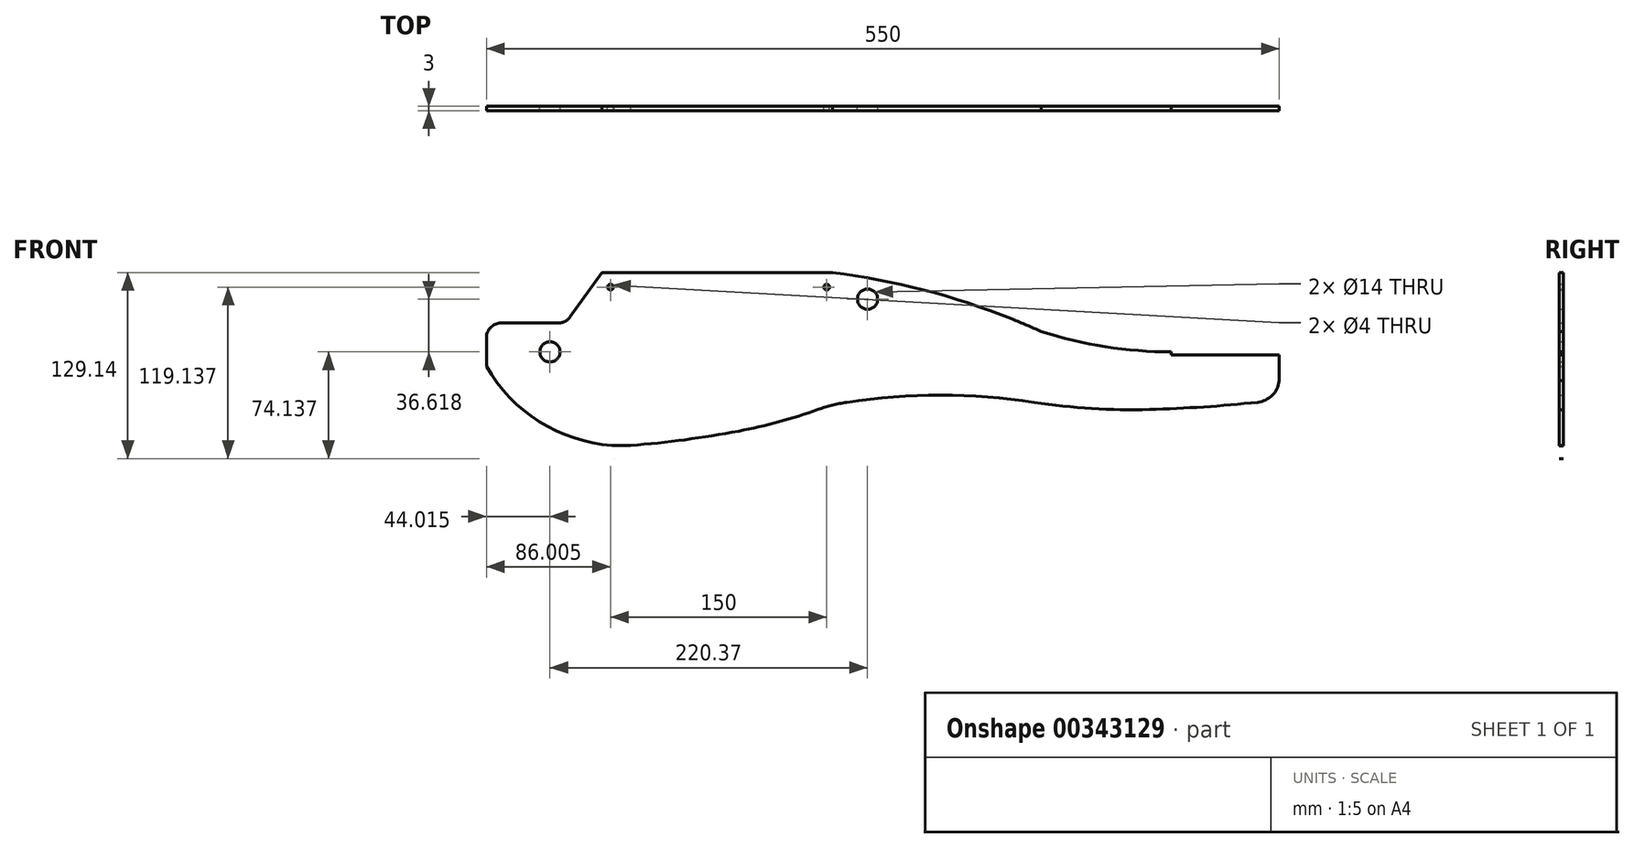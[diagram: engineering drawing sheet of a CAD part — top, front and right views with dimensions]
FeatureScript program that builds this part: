
annotation { "Feature Type Name" : "Feature", "Feature Type Description" : "" }
export const myFeature = defineFeature(function(context is Context, id is Id, definition is map)
    precondition{}
    {
        {
            var Q0;
            Q0=qCreatedBy(makeId("Front.planeOp"),FACE);
            var sketch = newSketch(context, id + "F0", { "sketchPlane" : qUnion([Q0])});
            skLineSegment(sketch, "E0", {"start": v(-85.37, -143.5) * mm, "end": v(-85.3, -135.5) * mm});
            skLineSegment(sketch, "E1", {"start": v(-60.46, -133.63) * mm, "end": v(-59.56, -141.58) * mm});
            skLineSegment(sketch, "E2", {"start": v(-107.58, -141) * mm, "end": v(-106.37, -133.08) * mm});
            skLineSegment(sketch, "E3", {"start": v(-111.58, -131.08) * mm, "end": v(-111.58, -155.3) * mm});
            skLineSegment(sketch, "E4", {"start": v(-19.81, -207.75) * mm, "end": v(-19.81, -42.75) * mm});
            skArc(sketch, "E5", {"start": v(2.74, -207.75) * mm, "mid": v(4.99, -150.27) * mm, "end": v(5.74, -92.75) * mm});
            skLineSegment(sketch, "E6", {"start": v(-164.34, -136.55) * mm, "end": v(-164.34, -172.55) * mm});
            skLineSegment(sketch, "E7", {"start": v(-144.97, -132.55) * mm, "end": v(-144.97, -180.55) * mm});
            skArc(sketch, "E8", {"start": v(-153.84, -148.05) * mm, "mid": v(-164.34, -137.55) * mm, "end": v(-174.84, -148.05) * mm});
            skLineSegment(sketch, "E9", {"start": v(-422.26, -217.75) * mm, "end": v(-422.26, 217.75) * mm});
            skLineSegment(sketch, "E10", {"start": v(242.74, -162.97) * mm, "end": v(242.74, -102.75) * mm});
            skLineSegment(sketch, "E11", {"start": v(254.74, -42.75) * mm, "end": v(254.74, -182.75) * mm});
            skLineSegment(sketch, "E12", {"start": v(-34.1, -204.75) * mm, "end": v(-34.1, -45.75) * mm});
            skLineSegment(sketch, "E13", {"start": v(-408.76, -42.75) * mm, "end": v(-408.76, -207.75) * mm});
            skLineSegment(sketch, "E14", {"start": v(-405.76, -42.75) * mm, "end": v(-405.76, -207.75) * mm});
            skLineSegment(sketch, "E15", {"start": v(-5.76, -42.75) * mm, "end": v(-5.76, -207.75) * mm});
            skLineSegment(sketch, "E16", {"start": v(-8.76, -42.75) * mm, "end": v(-8.76, -207.75) * mm});
            skLineSegment(sketch, "E17", {"start": v(-207.26, -215.75) * mm, "end": v(-207.26, -34.75) * mm});
            skCircle(sketch, "E18", {"center": v(78.1, -143) * mm, "radius": 7 * mm});
            skLineSegment(sketch, "E19", {"start": v(-195.26, -207.75) * mm, "end": v(-195.26, -42.75) * mm});
            skLineSegment(sketch, "E20", {"start": v(-192.26, -42.75) * mm, "end": v(-192.26, -207.75) * mm});
            skLineSegment(sketch, "E21", {"start": v(-219.26, -207.75) * mm, "end": v(-219.26, -42.75) * mm});
            skLineSegment(sketch, "E22", {"start": v(-222.26, -42.75) * mm, "end": v(-222.26, -207.75) * mm});
            skLineSegment(sketch, "E23", {"start": v(-7.26, -42.75) * mm, "end": v(-7.26, -207.75) * mm});
            skLineSegment(sketch, "E24", {"start": v(-407.26, -207.75) * mm, "end": v(-407.26, -42.75) * mm});
            skLineSegment(sketch, "E25", {"start": v(-234, -147.12) * mm, "end": v(-234, -139.24) * mm});
            skLineSegment(sketch, "E26", {"start": v(-394, -147.12) * mm, "end": v(-394, -139.24) * mm});
            skLineSegment(sketch, "E27", {"start": v(2.74, -42.75) * mm, "end": v(2.74, -207.75) * mm});
            skLineSegment(sketch, "E28", {"start": v(407.74, 217.75) * mm, "end": v(407.74, -217.75) * mm});
            skLineSegment(sketch, "E29", {"start": v(-92.77, -153.3) * mm, "end": v(-115.58, -153.3) * mm});
            skLineSegment(sketch, "E30", {"start": v(-407.26, -204.75) * mm, "end": v(-7.26, -204.75) * mm});
            skLineSegment(sketch, "E31", {"start": v(-407.26, -207.75) * mm, "end": v(-7.26, -207.75) * mm});
            skLineSegment(sketch, "E32", {"start": v(-422.26, -217.75) * mm, "end": v(407.74, -217.75) * mm});
            skCircle(sketch, "E33", {"center": v(-271.57, -159.18) * mm, "radius": 7 * mm});
            skLineSegment(sketch, "E34", {"start": v(-394, -148) * mm, "end": v(-234, -148) * mm});
            skLineSegment(sketch, "E35", {"start": v(-234, -172) * mm, "end": v(-394, -172) * mm});
            skLineSegment(sketch, "E36", {"start": v(-386.92, -141) * mm, "end": v(-234, -141) * mm});
            skLineSegment(sketch, "E37", {"start": v(-408.76, -207.75) * mm, "end": v(-407.26, -207.75) * mm});
            skLineSegment(sketch, "E38", {"start": v(-394, -172) * mm, "end": v(-394, -148) * mm});
            skLineSegment(sketch, "E39", {"start": v(-378.87, -172) * mm, "end": v(-384.76, -172) * mm});
            skLineSegment(sketch, "E40", {"start": v(-383, -164.94) * mm, "end": v(-383, -155.08) * mm});
            skLineSegment(sketch, "E41", {"start": v(-378.87, -148) * mm, "end": v(-384.76, -148) * mm});
            skLineSegment(sketch, "E42", {"start": v(-237.26, -202.75) * mm, "end": v(-177.26, -202.75) * mm});
            skLineSegment(sketch, "E43", {"start": v(-237.26, -207.75) * mm, "end": v(-237.26, -202.75) * mm});
            skLineSegment(sketch, "E44", {"start": v(-217.26, -217.75) * mm, "end": v(-217.26, -222.75) * mm});
            skLineSegment(sketch, "E45", {"start": v(-234, -172) * mm, "end": v(-234, -148) * mm});
            skLineSegment(sketch, "E46", {"start": v(-245.64, -157.09) * mm, "end": v(-257.64, -157.09) * mm});
            skLineSegment(sketch, "E47", {"start": v(-257.64, -157.09) * mm, "end": v(-254.38, -155.57) * mm});
            skLineSegment(sketch, "E48", {"start": v(-245.64, -157.09) * mm, "end": v(-248.9, -158.61) * mm});
            skLineSegment(sketch, "E49", {"start": v(-177.26, -202.75) * mm, "end": v(-177.26, -207.75) * mm});
            skLineSegment(sketch, "E50", {"start": v(-139.97, -157.55) * mm, "end": v(-149.97, -157.55) * mm});
            skLineSegment(sketch, "E51", {"start": v(-139.97, -172.55) * mm, "end": v(-149.97, -172.55) * mm});
            skArc(sketch, "E52", {"start": v(-158.84, -172.55) * mm, "mid": v(-155.1, -160.55) * mm, "end": v(-153.84, -148.05) * mm});
            skArc(sketch, "E53", {"start": v(-174.84, -148.05) * mm, "mid": v(-173.57, -160.55) * mm, "end": v(-169.84, -172.55) * mm});
            skLineSegment(sketch, "E54", {"start": v(-168.84, -157.55) * mm, "end": v(-168.84, -172.55) * mm});
            skLineSegment(sketch, "E55", {"start": v(-159.84, -157.55) * mm, "end": v(-159.84, -172.55) * mm});
            skLineSegment(sketch, "E56", {"start": v(-168.84, -172.55) * mm, "end": v(-169.84, -172.55) * mm});
            skLineSegment(sketch, "E57", {"start": v(-151.84, -180.55) * mm, "end": v(-176.84, -180.55) * mm});
            skLineSegment(sketch, "E58", {"start": v(-159.84, -172.55) * mm, "end": v(-158.84, -172.55) * mm});
            skLineSegment(sketch, "E59", {"start": v(-168.84, -175.55) * mm, "end": v(-168.84, -185.55) * mm});
            skLineSegment(sketch, "E60", {"start": v(-159.84, -175.55) * mm, "end": v(-159.84, -185.55) * mm});
            skLineSegment(sketch, "E61", {"start": v(-170.8, -143.7) * mm, "end": v(-168.69, -141.58) * mm});
            skCircle(sketch, "E62", {"center": v(-169.75, -142.65) * mm, "radius": 1 * mm});
            skLineSegment(sketch, "E63", {"start": v(-170.8, -141.58) * mm, "end": v(-168.69, -143.7) * mm});
            skLineSegment(sketch, "E64", {"start": v(-170.8, -152.4) * mm, "end": v(-168.69, -154.52) * mm});
            skCircle(sketch, "E65", {"center": v(-169.75, -153.46) * mm, "radius": 1 * mm});
            skLineSegment(sketch, "E66", {"start": v(-170.8, -154.52) * mm, "end": v(-168.69, -152.4) * mm});
            skLineSegment(sketch, "E67", {"start": v(-175.84, -148.05) * mm, "end": v(-152.84, -148.05) * mm});
            skLineSegment(sketch, "E68", {"start": v(-159.99, -141.58) * mm, "end": v(-157.87, -143.7) * mm});
            skCircle(sketch, "E69", {"center": v(-158.93, -142.65) * mm, "radius": 1 * mm});
            skLineSegment(sketch, "E70", {"start": v(-159.99, -143.7) * mm, "end": v(-157.87, -141.58) * mm});
            skLineSegment(sketch, "E71", {"start": v(-159.84, -157.55) * mm, "end": v(-168.84, -157.55) * mm});
            skCircle(sketch, "E72", {"center": v(-158.93, -153.46) * mm, "radius": 1 * mm});
            skLineSegment(sketch, "E73", {"start": v(-159.99, -154.52) * mm, "end": v(-157.87, -152.4) * mm});
            skLineSegment(sketch, "E74", {"start": v(-159.99, -152.4) * mm, "end": v(-157.87, -154.52) * mm});
            skCircle(sketch, "E75", {"center": v(-164.34, -148.05) * mm, "radius": 3 * mm});
            skCircle(sketch, "E76", {"center": v(-131.73, -173.26) * mm, "radius": 7 * mm});
            skLineSegment(sketch, "E77", {"start": v(2.74, -207.75) * mm, "end": v(225.72, -182.75) * mm});
            skArc(sketch, "E78", {"start": v(-107.58, -141) * mm, "mid": v(-83.7, -153.3) * mm, "end": v(-59.56, -141.58) * mm});
            skArc(sketch, "E79", {"start": v(-91.87, -143.25) * mm, "mid": v(-88.62, -143.43) * mm, "end": v(-85.37, -143.5) * mm});
            skArc(sketch, "E80", {"start": v(-90.32, -152.49) * mm, "mid": v(-87.93, -151.15) * mm, "end": v(-89.13, -148.68) * mm});
            skArc(sketch, "E81", {"start": v(-91.84, -143.25) * mm, "mid": v(-93.94, -144.78) * mm, "end": v(-92.77, -147.1) * mm});
            skLineSegment(sketch, "E82", {"start": v(-92.77, -147.1) * mm, "end": v(-89.07, -148.7) * mm});
            skLineSegment(sketch, "E83", {"start": v(-7.26, -217.75) * mm, "end": v(-7.26, -222.75) * mm});
            skLineSegment(sketch, "E84", {"start": v(-5.76, -207.75) * mm, "end": v(-7.26, -207.75) * mm});
            skLineSegment(sketch, "E85", {"start": v(89.26, -209.17) * mm, "end": v(189.26, -209.17) * mm});
            skLineSegment(sketch, "E86", {"start": v(89.26, -211.17) * mm, "end": v(189.26, -211.17) * mm});
            skLineSegment(sketch, "E87", {"start": v(89.26, -210.17) * mm, "end": v(189.26, -210.17) * mm});
            skLineSegment(sketch, "E88", {"start": v(89.26, -209.17) * mm, "end": v(89.26, -206.67) * mm});
            skLineSegment(sketch, "E89", {"start": v(89.26, -211.17) * mm, "end": v(89.26, -209.17) * mm});
            skLineSegment(sketch, "E90", {"start": v(94.26, -211.17) * mm, "end": v(94.26, -209.17) * mm});
            skLineSegment(sketch, "E91", {"start": v(93.26, -211.17) * mm, "end": v(93.26, -209.17) * mm});
            skLineSegment(sketch, "E92", {"start": v(92.26, -211.17) * mm, "end": v(92.26, -209.17) * mm});
            skLineSegment(sketch, "E93", {"start": v(91.26, -211.17) * mm, "end": v(91.26, -209.17) * mm});
            skLineSegment(sketch, "E94", {"start": v(90.26, -211.17) * mm, "end": v(90.26, -209.17) * mm});
            skLineSegment(sketch, "E95", {"start": v(99.26, -211.17) * mm, "end": v(99.26, -206.67) * mm});
            skLineSegment(sketch, "E96", {"start": v(98.26, -211.17) * mm, "end": v(98.26, -209.17) * mm});
            skLineSegment(sketch, "E97", {"start": v(109.26, -211.17) * mm, "end": v(109.26, -206.67) * mm});
            skLineSegment(sketch, "E98", {"start": v(97.26, -211.17) * mm, "end": v(97.26, -209.17) * mm});
            skLineSegment(sketch, "E99", {"start": v(96.26, -211.17) * mm, "end": v(96.26, -209.17) * mm});
            skLineSegment(sketch, "E100", {"start": v(95.26, -211.17) * mm, "end": v(95.26, -209.17) * mm});
            skLineSegment(sketch, "E101", {"start": v(129.26, -211.17) * mm, "end": v(129.26, -206.67) * mm});
            skLineSegment(sketch, "E102", {"start": v(119.26, -211.17) * mm, "end": v(119.26, -206.67) * mm});
            skLineSegment(sketch, "E103", {"start": v(72.73, -162.02) * mm, "end": v(76, -160.5) * mm});
            skLineSegment(sketch, "E104", {"start": v(84.73, -162.02) * mm, "end": v(72.73, -162.02) * mm});
            skLineSegment(sketch, "E105", {"start": v(84.73, -162.02) * mm, "end": v(81.47, -163.54) * mm});
            skLineSegment(sketch, "E106", {"start": v(149.26, -211.17) * mm, "end": v(149.26, -206.67) * mm});
            skLineSegment(sketch, "E107", {"start": v(139.26, -211.17) * mm, "end": v(139.26, -206.67) * mm});
            skLineSegment(sketch, "E108", {"start": v(159.26, -211.17) * mm, "end": v(159.26, -206.67) * mm});
            skLineSegment(sketch, "E109", {"start": v(169.26, -211.17) * mm, "end": v(169.26, -206.67) * mm});
            skLineSegment(sketch, "E110", {"start": v(202.74, -217.75) * mm, "end": v(202.74, -222.75) * mm});
            skLineSegment(sketch, "E111", {"start": v(189.26, -211.17) * mm, "end": v(189.26, -206.67) * mm});
            skLineSegment(sketch, "E112", {"start": v(179.26, -211.17) * mm, "end": v(179.26, -206.67) * mm});
            skLineSegment(sketch, "E113", {"start": v(222.74, -162.97) * mm, "end": v(236.88, -177.12) * mm});
            skArc(sketch, "E114", {"start": v(225.72, -182.75) * mm, "mid": v(237.9, -176.02) * mm, "end": v(242.74, -162.97) * mm});
            skLineSegment(sketch, "E115", {"start": v(244.74, -182.75) * mm, "end": v(254.74, -182.75) * mm});
            skLineSegment(sketch, "E116", {"start": v(222.74, -160.47) * mm, "end": v(222.74, -165.47) * mm});
            skLineSegment(sketch, "E117", {"start": v(225.24, -162.97) * mm, "end": v(220.24, -162.97) * mm});
            skLineSegment(sketch, "E118", {"start": v(-57.56, -128.27) * mm, "end": v(-109.58, -128.27) * mm});
            skLineSegment(sketch, "E119", {"start": v(-107.58, -133.08) * mm, "end": v(-115.58, -133.08) * mm});
            skLineSegment(sketch, "E120", {"start": v(168.53, 19.16) * mm, "end": v(-411.1, 19.16) * mm});
            skLineSegment(sketch, "E121", {"start": v(-103.29, 50.21) * mm, "end": v(-113.06, 50.21) * mm});
            skLineSegment(sketch, "E122", {"start": v(-103.29, 65.21) * mm, "end": v(-113.06, 65.21) * mm});
            skLineSegment(sketch, "E123", {"start": v(85.41, 128) * mm, "end": v(-332.58, 128) * mm});
            skLineSegment(sketch, "E124", {"start": v(-384.59, 86.54) * mm, "end": v(-80.66, 86.54) * mm});
            skLineSegment(sketch, "E125", {"start": v(-407.26, -17.75) * mm, "end": v(-7.26, -17.75) * mm});
            skLineSegment(sketch, "E126", {"start": v(-407.26, -45.75) * mm, "end": v(-7.26, -45.75) * mm});
            skLineSegment(sketch, "E127", {"start": v(-407.26, -42.75) * mm, "end": v(-7.26, -42.75) * mm});
            skArc(sketch, "E128", {"start": v(-20.12, 150.85) * mm, "mid": v(-81.3, 171) * mm, "end": v(-144.59, 183) * mm});
            skLineSegment(sketch, "E129", {"start": v(-144.59, 23.66) * mm, "end": v(165.41, 23.66) * mm});
            skLineSegment(sketch, "E130", {"start": v(-144.59, 17.66) * mm, "end": v(165.41, 17.66) * mm});
            skLineSegment(sketch, "E131", {"start": v(-144.59, 14.66) * mm, "end": v(165.41, 14.66) * mm});
            skLineSegment(sketch, "E132", {"start": v(-384.59, 203) * mm, "end": v(165.41, 203) * mm});
            skLineSegment(sketch, "E133", {"start": v(-122.26, 183) * mm, "end": v(150.8, 183) * mm});
            skLineSegment(sketch, "E134", {"start": v(165.41, 20.66) * mm, "end": v(-144.59, 20.66) * mm});
            skArc(sketch, "E135", {"start": v(-4.59, 93) * mm, "mid": v(-69.59, 98) * mm, "end": v(-134.59, 93) * mm});
            skLineSegment(sketch, "E136", {"start": v(-422.26, 217.75) * mm, "end": v(407.74, 217.75) * mm});
            skArc(sketch, "E137", {"start": v(-291.3, 70.87) * mm, "mid": v(-291.16, 70.87) * mm, "end": v(-291.02, 70.87) * mm});
            skArc(sketch, "E138", {"start": v(-280.24, 144.1) * mm, "mid": v(-309.44, 100) * mm, "end": v(-270.46, 64.26) * mm});
            skArc(sketch, "E139", {"start": v(-384.59, 118) * mm, "mid": v(-358.64, 87.23) * mm, "end": v(-323.25, 68.04) * mm});
            skLineSegment(sketch, "E140", {"start": v(-384.59, 115) * mm, "end": v(-384.59, 47.16) * mm});
            skArc(sketch, "E141", {"start": v(-284.59, 63) * mm, "mid": v(-246.95, 66.98) * mm, "end": v(-209.59, 73) * mm});
            skArc(sketch, "E142", {"start": v(-313.3, 65.36) * mm, "mid": v(-289.43, 53.06) * mm, "end": v(-265.28, 64.79) * mm});
            skLineSegment(sketch, "E143", {"start": v(-286.92, -7.87) * mm, "end": v(-258.15, -7.87) * mm});
            skLineSegment(sketch, "E144", {"start": v(-264.24, 46.33) * mm, "end": v(-274.59, 33.66) * mm});
            skLineSegment(sketch, "E145", {"start": v(-284.59, 13.66) * mm, "end": v(-264.59, 13.66) * mm});
            skLineSegment(sketch, "E146", {"start": v(-284.59, 33.66) * mm, "end": v(-264.59, 33.66) * mm});
            skLineSegment(sketch, "E147", {"start": v(-274.59, 9.66) * mm, "end": v(-264.59, 9.66) * mm});
            skLineSegment(sketch, "E148", {"start": v(-272.59, 5.66) * mm, "end": v(-266.59, 5.66) * mm});
            skArc(sketch, "E149", {"start": v(-234, -102.2) * mm, "mid": v(-288.67, -92.34) * mm, "end": v(-344, -87.2) * mm});
            skLineSegment(sketch, "E150", {"start": v(-394, -102.2) * mm, "end": v(-234, -102.2) * mm});
            skArc(sketch, "E151", {"start": v(-233.33, -99.28) * mm, "mid": v(-288.26, -89.37) * mm, "end": v(-343.84, -84.21) * mm});
            skLineSegment(sketch, "E152", {"start": v(-389.62, -99.2) * mm, "end": v(-248.04, -99.2) * mm});
            skLineSegment(sketch, "E153", {"start": v(-284.59, 14.66) * mm, "end": v(-264.59, 14.66) * mm});
            skLineSegment(sketch, "E154", {"start": v(-284.59, 17.66) * mm, "end": v(-264.59, 17.66) * mm});
            skLineSegment(sketch, "E155", {"start": v(-284.59, 23.66) * mm, "end": v(-264.59, 23.66) * mm});
            skLineSegment(sketch, "E156", {"start": v(-264.59, 20.66) * mm, "end": v(-284.59, 20.66) * mm});
            skLineSegment(sketch, "E157", {"start": v(-407.26, -39.75) * mm, "end": v(-407.26, -14.75) * mm});
            skArc(sketch, "E158", {"start": v(-344, -87.2) * mm, "mid": v(-370.3, -90.35) * mm, "end": v(-394, -102.2) * mm});
            skArc(sketch, "E159", {"start": v(-343.84, -84.21) * mm, "mid": v(-370.27, -87.22) * mm, "end": v(-394.26, -98.7) * mm});
            skLineSegment(sketch, "E160", {"start": v(-390.25, -83.08) * mm, "end": v(-394.4, -99.99) * mm});
            skLineSegment(sketch, "E161", {"start": v(-393.47, -98.16) * mm, "end": v(-391.72, -100.59) * mm});
            skArc(sketch, "E162", {"start": v(-394.26, -98.7) * mm, "mid": v(-395.13, -100.54) * mm, "end": v(-394, -102.2) * mm});
            skLineSegment(sketch, "E163", {"start": v(-407.26, -42.75) * mm, "end": v(-408.76, -42.75) * mm});
            skLineSegment(sketch, "E164", {"start": v(-407.26, -42.75) * mm, "end": v(-405.26, -42.75) * mm});
            skLineSegment(sketch, "E165", {"start": v(-390.25, -83.08) * mm, "end": v(-381.94, -83.08) * mm});
            skLineSegment(sketch, "E166", {"start": v(-303.46, -80.13) * mm, "end": v(-305.53, -88.59) * mm});
            skLineSegment(sketch, "E167", {"start": v(-320.4, -100.94) * mm, "end": v(-303.46, -80.13) * mm});
            skLineSegment(sketch, "E168", {"start": v(-303.46, -80.13) * mm, "end": v(-278.38, -80.13) * mm});
            skLineSegment(sketch, "E169", {"start": v(-385.2, 31) * mm, "end": v(-314.86, 31) * mm});
            skLineSegment(sketch, "E170", {"start": v(-373.46, 14.66) * mm, "end": v(-304.59, 14.66) * mm});
            skLineSegment(sketch, "E171", {"start": v(-373.3, 23.66) * mm, "end": v(-304.59, 23.66) * mm});
            skLineSegment(sketch, "E172", {"start": v(-373.4, 17.66) * mm, "end": v(-304.59, 17.66) * mm});
            skLineSegment(sketch, "E173", {"start": v(-304.59, 20.66) * mm, "end": v(-373.36, 20.66) * mm});
            skLineSegment(sketch, "E174", {"start": v(-403.86, 18.63) * mm, "end": v(-403.81, 20.73) * mm});
            skLineSegment(sketch, "E175", {"start": v(-400.92, 18.57) * mm, "end": v(-400.88, 20.67) * mm});
            skLineSegment(sketch, "E176", {"start": v(-411.1, 19.8) * mm, "end": v(-352.96, 18.78) * mm});
            skLineSegment(sketch, "E177", {"start": v(-374.7, 29.16) * mm, "end": v(-375.06, 9.16) * mm});
            skLineSegment(sketch, "E178", {"start": v(-373.2, 29.13) * mm, "end": v(-373.56, 9.14) * mm});
            skLineSegment(sketch, "E179", {"start": v(-374.72, 28.16) * mm, "end": v(-375.04, 10.16) * mm});
            skLineSegment(sketch, "E180", {"start": v(-377.34, 10.2) * mm, "end": v(-377.02, 28.2) * mm});
            skLineSegment(sketch, "E181", {"start": v(-387, 12.22) * mm, "end": v(-386.76, 26.52) * mm});
            skLineSegment(sketch, "E182", {"start": v(-394.4, 12.35) * mm, "end": v(-394.15, 26.65) * mm});
            skLineSegment(sketch, "E183", {"start": v(-400.97, 15.42) * mm, "end": v(-398.47, 15.37) * mm});
            skLineSegment(sketch, "E184", {"start": v(-400.82, 23.82) * mm, "end": v(-398.33, 23.77) * mm});
            skLineSegment(sketch, "E185", {"start": v(-400.97, 15.42) * mm, "end": v(-400.82, 23.82) * mm});
            skLineSegment(sketch, "E186", {"start": v(-403.21, 17.76) * mm, "end": v(-403.14, 21.56) * mm});
            skLineSegment(sketch, "E187", {"start": v(-403.14, 21.56) * mm, "end": v(-400.86, 21.52) * mm});
            skLineSegment(sketch, "E188", {"start": v(-403.21, 17.76) * mm, "end": v(-400.93, 17.72) * mm});
            skLineSegment(sketch, "E189", {"start": v(-382.12, 14.29) * mm, "end": v(-381.94, 24.29) * mm});
            skLineSegment(sketch, "E190", {"start": v(-386.83, 22.37) * mm, "end": v(-381.98, 22.28) * mm});
            skLineSegment(sketch, "E191", {"start": v(-398.47, 15.37) * mm, "end": v(-398.33, 23.77) * mm});
            skLineSegment(sketch, "E192", {"start": v(-381.94, 24.29) * mm, "end": v(-377.1, 24.2) * mm});
            skLineSegment(sketch, "E193", {"start": v(-394.15, 26.65) * mm, "end": v(-386.76, 26.52) * mm});
            skLineSegment(sketch, "E194", {"start": v(-377.02, 28.2) * mm, "end": v(-374.72, 28.16) * mm});
            skLineSegment(sketch, "E195", {"start": v(-382.12, 14.29) * mm, "end": v(-377.27, 14.2) * mm});
            skLineSegment(sketch, "E196", {"start": v(-395.8, 18.03) * mm, "end": v(-395.75, 21.03) * mm});
            skLineSegment(sketch, "E197", {"start": v(-396.8, 18.04) * mm, "end": v(-396.75, 21.04) * mm});
            skLineSegment(sketch, "E198", {"start": v(-395.75, 21.03) * mm, "end": v(-394.25, 21) * mm});
            skLineSegment(sketch, "E199", {"start": v(-398.37, 21.47) * mm, "end": v(-396.75, 21.04) * mm});
            skLineSegment(sketch, "E200", {"start": v(-396.8, 18.8) * mm, "end": v(-395.8, 18.78) * mm});
            skLineSegment(sketch, "E201", {"start": v(-396.77, 20.3) * mm, "end": v(-395.77, 20.28) * mm});
            skLineSegment(sketch, "E202", {"start": v(-386.93, 16.38) * mm, "end": v(-382.08, 16.3) * mm});
            skLineSegment(sketch, "E203", {"start": v(-395.8, 18.03) * mm, "end": v(-394.3, 18) * mm});
            skLineSegment(sketch, "E204", {"start": v(-398.43, 17.67) * mm, "end": v(-396.8, 18.04) * mm});
            skLineSegment(sketch, "E205", {"start": v(-394.4, 12.35) * mm, "end": v(-387, 12.22) * mm});
            skLineSegment(sketch, "E206", {"start": v(-377.34, 10.2) * mm, "end": v(-375.04, 10.16) * mm});
            skLineSegment(sketch, "E207", {"start": v(-384.59, 23.66) * mm, "end": v(-384.59, 14.66) * mm});
            skLineSegment(sketch, "E208", {"start": v(-401.47, -2.69) * mm, "end": v(-400.92, 18.57) * mm});
            skLineSegment(sketch, "E209", {"start": v(-403.86, 18.63) * mm, "end": v(-403.87, -3.74) * mm});
            skLineSegment(sketch, "E210", {"start": v(-375.06, 9.16) * mm, "end": v(-373.56, 9.14) * mm});
            skLineSegment(sketch, "E211", {"start": v(-384.59, 14.66) * mm, "end": v(-374.96, 14.66) * mm});
            skLineSegment(sketch, "E212", {"start": v(-400.63, 49.57) * mm, "end": v(-400.88, 20.68) * mm});
            skLineSegment(sketch, "E213", {"start": v(-403.82, 20.73) * mm, "end": v(-402.8, 50.28) * mm});
            skLineSegment(sketch, "E214", {"start": v(-385.2, 31) * mm, "end": v(-388.81, 26.59) * mm});
            skLineSegment(sketch, "E215", {"start": v(-374.7, 29.16) * mm, "end": v(-373.2, 29.13) * mm});
            skLineSegment(sketch, "E216", {"start": v(-384.59, 23.66) * mm, "end": v(-374.8, 23.66) * mm});
            skLineSegment(sketch, "E217", {"start": v(-292.43, 24.5) * mm, "end": v(-292.43, 12.5) * mm});
            skLineSegment(sketch, "E218", {"start": v(-304.59, 4.16) * mm, "end": v(-304.59, 34.16) * mm});
            skLineSegment(sketch, "E219", {"start": v(-284.59, 34.16) * mm, "end": v(-284.59, 4.16) * mm});
            skLineSegment(sketch, "E220", {"start": v(-300.59, 4.16) * mm, "end": v(-300.59, 34.16) * mm});
            skLineSegment(sketch, "E221", {"start": v(-296.59, 34.16) * mm, "end": v(-296.59, 4.16) * mm});
            skLineSegment(sketch, "E222", {"start": v(-337.09, 20.66) * mm, "end": v(-337.09, 17.66) * mm});
            skLineSegment(sketch, "E223", {"start": v(-342.09, 20.66) * mm, "end": v(-342.09, 17.66) * mm});
            skCircle(sketch, "E224", {"center": v(-313.37, 6.52) * mm, "radius": 7 * mm});
            skLineSegment(sketch, "E225", {"start": v(-286.92, -7.87) * mm, "end": v(-298.59, 1.66) * mm});
            skLineSegment(sketch, "E226", {"start": v(-284.59, 4.16) * mm, "end": v(-304.59, 4.16) * mm});
            skLineSegment(sketch, "E227", {"start": v(-296.59, 4.16) * mm, "end": v(-296.59, 1.66) * mm});
            skLineSegment(sketch, "E228", {"start": v(-300.59, 4.16) * mm, "end": v(-300.59, 1.66) * mm});
            skLineSegment(sketch, "E229", {"start": v(-296.59, 1.66) * mm, "end": v(-300.59, 1.66) * mm});
            skLineSegment(sketch, "E230", {"start": v(-292.43, 12.5) * mm, "end": v(-293.95, 15.76) * mm});
            skLineSegment(sketch, "E231", {"start": v(-274.59, 9.66) * mm, "end": v(-274.59, 13.66) * mm});
            skLineSegment(sketch, "E232", {"start": v(-274.59, 11.66) * mm, "end": v(-277.59, 11.66) * mm});
            skLineSegment(sketch, "E233", {"start": v(-277.59, 11.66) * mm, "end": v(-277.59, 13.66) * mm});
            skLineSegment(sketch, "E234", {"start": v(-272.59, 5.66) * mm, "end": v(-272.59, 9.66) * mm});
            skArc(sketch, "E235", {"start": v(-323.25, 68.04) * mm, "mid": v(-304.15, 63.77) * mm, "end": v(-284.59, 63) * mm});
            skLineSegment(sketch, "E236", {"start": v(-292.43, 24.5) * mm, "end": v(-290.91, 21.23) * mm});
            skLineSegment(sketch, "E237", {"start": v(-304.59, 34.16) * mm, "end": v(-284.59, 34.16) * mm});
            skLineSegment(sketch, "E238", {"start": v(-296.59, 36.66) * mm, "end": v(-296.59, 34.16) * mm});
            skLineSegment(sketch, "E239", {"start": v(-300.59, 36.66) * mm, "end": v(-300.59, 34.16) * mm});
            skLineSegment(sketch, "E240", {"start": v(-300.59, 36.66) * mm, "end": v(-296.59, 36.66) * mm});
            skArc(sketch, "E241", {"start": v(-296.04, 53.88) * mm, "mid": v(-296.02, 53.88) * mm, "end": v(-296, 53.87) * mm});
            skLineSegment(sketch, "E242", {"start": v(-294.84, 57.69) * mm, "end": v(-294.78, 57.66) * mm});
            skArc(sketch, "E243", {"start": v(-297.56, 63.12) * mm, "mid": v(-297.57, 63.12) * mm, "end": v(-297.59, 63.12) * mm});
            skLineSegment(sketch, "E244", {"start": v(-291.02, 70.69) * mm, "end": v(-291.02, 70.87) * mm});
            skCircle(sketch, "E245", {"center": v(-178.82, -29.52) * mm, "radius": 7 * mm});
            skLineSegment(sketch, "E246", {"start": v(-167.26, -35.68) * mm, "end": v(-167.26, -28.6) * mm});
            skLineSegment(sketch, "E247", {"start": v(-222.26, -40.75) * mm, "end": v(-222.26, -29.75) * mm});
            skLineSegment(sketch, "E248", {"start": v(-192.26, -40.75) * mm, "end": v(-192.26, -29.75) * mm});
            skLineSegment(sketch, "E249", {"start": v(-230.2, -56.53) * mm, "end": v(-184.33, -56.53) * mm});
            skLineSegment(sketch, "E250", {"start": v(-237.26, -47.75) * mm, "end": v(-177.26, -47.75) * mm});
            skCircle(sketch, "E251", {"center": v(-258, -112.32) * mm, "radius": 7 * mm});
            skLineSegment(sketch, "E252", {"start": v(-262.84, -107.28) * mm, "end": v(-269.08, -100.79) * mm});
            skLineSegment(sketch, "E253", {"start": v(-233.33, -99.28) * mm, "end": v(-234, -102.2) * mm});
            skLineSegment(sketch, "E254", {"start": v(-236.26, -98.63) * mm, "end": v(-236.92, -101.55) * mm});
            skLineSegment(sketch, "E255", {"start": v(-237.32, -90.65) * mm, "end": v(-234.94, -100.3) * mm});
            skLineSegment(sketch, "E256", {"start": v(-245.93, -90.65) * mm, "end": v(-237.32, -90.65) * mm});
            skLineSegment(sketch, "E257", {"start": v(-237.26, -49.75) * mm, "end": v(-237.26, -59.53) * mm});
            skLineSegment(sketch, "E258", {"start": v(-237.26, -42.75) * mm, "end": v(-237.26, -47.75) * mm});
            skLineSegment(sketch, "E259", {"start": v(-139.97, -137.55) * mm, "end": v(-149.97, -137.55) * mm});
            skLineSegment(sketch, "E260", {"start": v(-149.34, -132.9) * mm, "end": v(-179.34, -132.9) * mm});
            skLineSegment(sketch, "E261", {"start": v(-174.34, -127.9) * mm, "end": v(-174.34, -137.9) * mm});
            skLineSegment(sketch, "E262", {"start": v(-154.34, -127.88) * mm, "end": v(-154.34, -137.88) * mm});
            skCircle(sketch, "E263", {"center": v(-180.24, -96.46) * mm, "radius": 7 * mm});
            skLineSegment(sketch, "E264", {"start": v(-110.07, -90.7) * mm, "end": v(-113.33, -92.22) * mm});
            skLineSegment(sketch, "E265", {"start": v(-122.07, -90.7) * mm, "end": v(-118.8, -89.18) * mm});
            skLineSegment(sketch, "E266", {"start": v(-110.07, -90.7) * mm, "end": v(-122.07, -90.7) * mm});
            skLineSegment(sketch, "E267", {"start": v(-167.26, -54.82) * mm, "end": v(-167.26, -61.9) * mm});
            skLineSegment(sketch, "E268", {"start": v(-175.26, -47.75) * mm, "end": v(-165.5, -47.75) * mm});
            skLineSegment(sketch, "E269", {"start": v(-177.26, -49.75) * mm, "end": v(-177.26, -59.53) * mm});
            skLineSegment(sketch, "E270", {"start": v(-177.26, -47.75) * mm, "end": v(-177.26, -42.75) * mm});
            skLineSegment(sketch, "E271", {"start": v(-167.26, -47.75) * mm, "end": v(-167.26, -42.75) * mm});
            skCircle(sketch, "E272", {"center": v(-116.7, -71.68) * mm, "radius": 7 * mm});
            skLineSegment(sketch, "E273", {"start": v(-244.59, 23.66) * mm, "end": v(-164.59, 23.66) * mm});
            skLineSegment(sketch, "E274", {"start": v(-244.59, 17.66) * mm, "end": v(-164.59, 17.66) * mm});
            skLineSegment(sketch, "E275", {"start": v(-244.59, 14.66) * mm, "end": v(-164.59, 14.66) * mm});
            skLineSegment(sketch, "E276", {"start": v(-164.59, 20.66) * mm, "end": v(-244.59, 20.66) * mm});
            skLineSegment(sketch, "E277", {"start": v(-234.6, 28.66) * mm, "end": v(-234.6, 4.66) * mm});
            skLineSegment(sketch, "E278", {"start": v(-264.59, 4.16) * mm, "end": v(-264.59, 34.16) * mm});
            skLineSegment(sketch, "E279", {"start": v(-244.59, 34.16) * mm, "end": v(-244.59, 4.16) * mm});
            skLineSegment(sketch, "E280", {"start": v(-244.59, 4.16) * mm, "end": v(-264.59, 4.16) * mm});
            skLineSegment(sketch, "E281", {"start": v(-266.59, 5.66) * mm, "end": v(-266.59, 9.66) * mm});
            skLineSegment(sketch, "E282", {"start": v(-244.59, 4.66) * mm, "end": v(-234.6, 4.66) * mm});
            skLineSegment(sketch, "E283", {"start": v(-199.33, -32.75) * mm, "end": v(-215.2, -32.75) * mm});
            skLineSegment(sketch, "E284", {"start": v(-264.24, 46.33) * mm, "end": v(-208.56, 46.33) * mm});
            skLineSegment(sketch, "E285", {"start": v(-264.24, 46.33) * mm, "end": v(-239.6, 32.66) * mm});
            skLineSegment(sketch, "E286", {"start": v(-264.59, 34.16) * mm, "end": v(-244.59, 34.16) * mm});
            skLineSegment(sketch, "E287", {"start": v(-257.51, 26.66) * mm, "end": v(-251.66, 26.66) * mm});
            skLineSegment(sketch, "E288", {"start": v(-244.6, 24.66) * mm, "end": v(-230.6, 24.66) * mm});
            skLineSegment(sketch, "E289", {"start": v(-230.6, 24.66) * mm, "end": v(-230.6, 23.66) * mm});
            skLineSegment(sketch, "E290", {"start": v(-244.6, 28.66) * mm, "end": v(-234.6, 28.66) * mm});
            skLineSegment(sketch, "E291", {"start": v(-242.6, 32.66) * mm, "end": v(-242.6, 28.66) * mm});
            skLineSegment(sketch, "E292", {"start": v(-242.6, 32.66) * mm, "end": v(-236.6, 32.66) * mm});
            skLineSegment(sketch, "E293", {"start": v(-236.6, 32.66) * mm, "end": v(-236.6, 28.66) * mm});
            skLineSegment(sketch, "E294", {"start": v(-234.6, 23.66) * mm, "end": v(-230.6, 23.66) * mm});
            skLineSegment(sketch, "E295", {"start": v(-133.78, 1.66) * mm, "end": v(-133.78, 36.66) * mm});
            skLineSegment(sketch, "E296", {"start": v(-164.59, 4.16) * mm, "end": v(-164.59, 34.16) * mm});
            skLineSegment(sketch, "E297", {"start": v(-144.59, 34.16) * mm, "end": v(-144.59, 4.16) * mm});
            skLineSegment(sketch, "E298", {"start": v(-150.59, 4.16) * mm, "end": v(-150.59, 34.16) * mm});
            skLineSegment(sketch, "E299", {"start": v(-146.59, 34.16) * mm, "end": v(-146.59, 4.16) * mm});
            skLineSegment(sketch, "E300", {"start": v(-156.63, 4.16) * mm, "end": v(-156.63, 34.16) * mm});
            skLineSegment(sketch, "E301", {"start": v(-146.59, 1.66) * mm, "end": v(-150.59, 1.66) * mm});
            skLineSegment(sketch, "E302", {"start": v(-144.59, 4.16) * mm, "end": v(-164.59, 4.16) * mm});
            skLineSegment(sketch, "E303", {"start": v(-150.59, 4.16) * mm, "end": v(-150.59, 1.66) * mm});
            skLineSegment(sketch, "E304", {"start": v(-143.78, 1.66) * mm, "end": v(-131.78, 1.66) * mm});
            skLineSegment(sketch, "E305", {"start": v(-146.59, 4.16) * mm, "end": v(-146.59, 1.66) * mm});
            skLineSegment(sketch, "E306", {"start": v(-152.42, 41.36) * mm, "end": v(-148.59, 36.66) * mm});
            skLineSegment(sketch, "E307", {"start": v(-150.59, 36.66) * mm, "end": v(-146.59, 36.66) * mm});
            skLineSegment(sketch, "E308", {"start": v(-164.59, 34.16) * mm, "end": v(-144.59, 34.16) * mm});
            skLineSegment(sketch, "E309", {"start": v(-184.37, 41.36) * mm, "end": v(-152.42, 41.36) * mm});
            skLineSegment(sketch, "E310", {"start": v(-150.59, 36.66) * mm, "end": v(-150.59, 34.16) * mm});
            skLineSegment(sketch, "E311", {"start": v(-143.78, 36.66) * mm, "end": v(-131.78, 36.66) * mm});
            skLineSegment(sketch, "E312", {"start": v(-146.59, 36.66) * mm, "end": v(-146.59, 34.16) * mm});
            skLineSegment(sketch, "E313", {"start": v(-111.29, 43.14) * mm, "end": v(-111.29, 36.07) * mm});
            skLineSegment(sketch, "E314", {"start": v(-111.29, 50.21) * mm, "end": v(-111.29, 65.21) * mm});
            skLineSegment(sketch, "E315", {"start": v(-144.59, 183) * mm, "end": v(-280.24, 144.1) * mm});
            skArc(sketch, "E316", {"start": v(-330.16, 149.12) * mm, "mid": v(-295.52, 152.48) * mm, "end": v(-278.81, 183) * mm});
            skLineSegment(sketch, "E317", {"start": v(-304.59, 183) * mm, "end": v(-144.59, 183) * mm});
            skLineSegment(sketch, "E318", {"start": v(-384.59, 193) * mm, "end": v(-144.59, 193) * mm});
            skLineSegment(sketch, "E319", {"start": v(-406.06, 197.82) * mm, "end": v(-401.25, 136.7) * mm});
            skLineSegment(sketch, "E320", {"start": v(-404.18, 136.49) * mm, "end": v(-407.41, 197.34) * mm});
            skFitSpline(sketch, "E321", {"points": [v(-407.41, 197.34) * mm, v(-407.4, 197.57) * mm, v(-407.4, 197.87) * mm, v(-407.38, 198.27) * mm, v(-407.25, 198.59) * mm, v(-406.94, 198.85) * mm, v(-406.57, 198.94) * mm, v(-406.2, 198.82) * mm, v(-406.1, 198.34) * mm, v(-406.07, 198) * mm, v(-406.06, 197.82) * mm]});
            skLineSegment(sketch, "E322", {"start": v(-404.03, 134.4) * mm, "end": v(-398.76, 73.68) * mm});
            skLineSegment(sketch, "E323", {"start": v(-397.36, 73.4) * mm, "end": v(-401.1, 134.59) * mm});
            skFitSpline(sketch, "E324", {"points": [v(-398.76, 73.68) * mm, v(-398.73, 73.45) * mm, v(-398.68, 73.16) * mm, v(-398.6, 72.76) * mm, v(-398.43, 72.47) * mm, v(-398.08, 72.26) * mm, v(-397.71, 72.2) * mm, v(-397.36, 72.39) * mm, v(-397.32, 72.88) * mm, v(-397.35, 73.2) * mm, v(-397.36, 73.4) * mm]});
            skLineSegment(sketch, "E325", {"start": v(-401.25, 136.7) * mm, "end": v(-401.1, 134.6) * mm});
            skLineSegment(sketch, "E326", {"start": v(-404.18, 136.49) * mm, "end": v(-404.03, 134.4) * mm});
            skLineSegment(sketch, "E327", {"start": v(-384.59, 144) * mm, "end": v(-384.59, 194.77) * mm});
            skLineSegment(sketch, "E328", {"start": v(-304.59, 181) * mm, "end": v(-304.59, 156.24) * mm});
            skLineSegment(sketch, "E329", {"start": v(-287.59, 173) * mm, "end": v(-287.59, 183) * mm});
            skLineSegment(sketch, "E330", {"start": v(-304.59, 183) * mm, "end": v(-326.6, 152.2) * mm});
            skLineSegment(sketch, "E331", {"start": v(-298.59, 178) * mm, "end": v(-298.59, 166) * mm});
            skLineSegment(sketch, "E332", {"start": v(-348.58, 128) * mm, "end": v(-412.77, 128) * mm});
            skLineSegment(sketch, "E333", {"start": v(-334.73, 148) * mm, "end": v(-374.59, 148) * mm});
            skLineSegment(sketch, "E334", {"start": v(-372, 113) * mm, "end": v(-374.45, 148) * mm});
            skLineSegment(sketch, "E335", {"start": v(-373.5, 112.9) * mm, "end": v(-375.95, 147.91) * mm});
            skLineSegment(sketch, "E336", {"start": v(-384.59, 138) * mm, "end": v(-384.59, 118) * mm});
            skLineSegment(sketch, "E337", {"start": v(-372, 113) * mm, "end": v(-373.5, 112.9) * mm});
            skLineSegment(sketch, "E338", {"start": v(-374.6, 128.49) * mm, "end": v(-375.85, 146.45) * mm});
            skLineSegment(sketch, "E339", {"start": v(-378.14, 146.29) * mm, "end": v(-376.88, 128.33) * mm});
            skLineSegment(sketch, "E340", {"start": v(-387.69, 143.76) * mm, "end": v(-386.69, 129.5) * mm});
            skLineSegment(sketch, "E341", {"start": v(-395.07, 143.25) * mm, "end": v(-394.07, 128.98) * mm});
            skLineSegment(sketch, "E342", {"start": v(-401.47, 139.84) * mm, "end": v(-398.97, 140.02) * mm});
            skLineSegment(sketch, "E343", {"start": v(-400.88, 131.46) * mm, "end": v(-398.39, 131.64) * mm});
            skLineSegment(sketch, "E344", {"start": v(-401.47, 139.84) * mm, "end": v(-400.88, 131.46) * mm});
            skLineSegment(sketch, "E345", {"start": v(-403.58, 137.39) * mm, "end": v(-403.32, 133.6) * mm});
            skLineSegment(sketch, "E346", {"start": v(-403.32, 133.6) * mm, "end": v(-401.04, 133.76) * mm});
            skLineSegment(sketch, "E347", {"start": v(-403.58, 137.39) * mm, "end": v(-401.3, 137.55) * mm});
            skLineSegment(sketch, "E348", {"start": v(-382.7, 141.96) * mm, "end": v(-382, 131.98) * mm});
            skLineSegment(sketch, "E349", {"start": v(-386.98, 133.64) * mm, "end": v(-382.14, 133.98) * mm});
            skLineSegment(sketch, "E350", {"start": v(-398.97, 140.02) * mm, "end": v(-398.39, 131.64) * mm});
            skLineSegment(sketch, "E351", {"start": v(-382, 131.98) * mm, "end": v(-377.16, 132.32) * mm});
            skLineSegment(sketch, "E352", {"start": v(-394.07, 128.98) * mm, "end": v(-386.69, 129.5) * mm});
            skLineSegment(sketch, "E353", {"start": v(-376.88, 128.33) * mm, "end": v(-374.6, 128.49) * mm});
            skLineSegment(sketch, "E354", {"start": v(-382.7, 141.96) * mm, "end": v(-377.86, 142.3) * mm});
            skLineSegment(sketch, "E355", {"start": v(-396.17, 137.5) * mm, "end": v(-395.96, 134.51) * mm});
            skLineSegment(sketch, "E356", {"start": v(-397.17, 137.44) * mm, "end": v(-396.96, 134.44) * mm});
            skLineSegment(sketch, "E357", {"start": v(-395.96, 134.51) * mm, "end": v(-394.47, 134.62) * mm});
            skLineSegment(sketch, "E358", {"start": v(-398.55, 133.93) * mm, "end": v(-396.96, 134.44) * mm});
            skLineSegment(sketch, "E359", {"start": v(-397.12, 136.69) * mm, "end": v(-396.12, 136.76) * mm});
            skLineSegment(sketch, "E360", {"start": v(-397.01, 135.2) * mm, "end": v(-396.01, 135.26) * mm});
            skLineSegment(sketch, "E361", {"start": v(-387.4, 139.62) * mm, "end": v(-382.56, 139.96) * mm});
            skLineSegment(sketch, "E362", {"start": v(-396.17, 137.5) * mm, "end": v(-394.68, 137.61) * mm});
            skLineSegment(sketch, "E363", {"start": v(-398.81, 137.72) * mm, "end": v(-397.17, 137.44) * mm});
            skLineSegment(sketch, "E364", {"start": v(-395.07, 143.25) * mm, "end": v(-387.69, 143.76) * mm});
            skLineSegment(sketch, "E365", {"start": v(-378.14, 146.29) * mm, "end": v(-375.85, 146.45) * mm});
            skLineSegment(sketch, "E366", {"start": v(-412.77, 134.84) * mm, "end": v(-354.7, 138.9) * mm});
            skLineSegment(sketch, "E367", {"start": v(-384.59, 148.9) * mm, "end": v(-384.59, 164.77) * mm});
            skLineSegment(sketch, "E368", {"start": v(-373.05, 127.97) * mm, "end": v(-384.59, 127.17) * mm});
            skArc(sketch, "E369", {"start": v(-374.59, 148) * mm, "mid": v(-381.66, 145.08) * mm, "end": v(-384.59, 138) * mm});
            skCircle(sketch, "E370", {"center": v(-340.58, 128) * mm, "radius": 7 * mm});
            skLineSegment(sketch, "E371", {"start": v(-311.66, 165) * mm, "end": v(-318.73, 165) * mm});
            skArc(sketch, "E372", {"start": v(-334.73, 148) * mm, "mid": v(-330.16, 149.12) * mm, "end": v(-326.6, 152.2) * mm});
            skLineSegment(sketch, "E373", {"start": v(-304.59, 173.12) * mm, "end": v(-304.59, 163.24) * mm});
            skLineSegment(sketch, "E374", {"start": v(-303.59, 173) * mm, "end": v(-289.59, 173) * mm});
            skLineSegment(sketch, "E375", {"start": v(-291.51, 165) * mm, "end": v(-284.44, 165) * mm});
            skLineSegment(sketch, "E376", {"start": v(-297.51, 158) * mm, "end": v(-271.66, 158) * mm});
            skLineSegment(sketch, "E377", {"start": v(-292.7, 173) * mm, "end": v(-285.82, 173) * mm});
            skCircle(sketch, "E378", {"center": v(-298.59, 173) * mm, "radius": 2 * mm});
            skLineSegment(sketch, "E379", {"start": v(-298.59, 165) * mm, "end": v(-304.59, 165) * mm});
            skLineSegment(sketch, "E380", {"start": v(-304.59, 172.12) * mm, "end": v(-304.59, 163.24) * mm});
            skLineSegment(sketch, "E381", {"start": v(-298.59, 172.12) * mm, "end": v(-298.59, 163.24) * mm});
            skLineSegment(sketch, "E382", {"start": v(-287.59, 165.94) * mm, "end": v(-287.59, 158.87) * mm});
            skLineSegment(sketch, "E383", {"start": v(-384.59, 178.9) * mm, "end": v(-384.59, 206) * mm});
            skLineSegment(sketch, "E384", {"start": v(-304.59, 185) * mm, "end": v(-284.59, 185) * mm});
            skLineSegment(sketch, "E385", {"start": v(-304.59, 185) * mm, "end": v(-304.59, 183) * mm});
            skLineSegment(sketch, "E386", {"start": v(-304.59, 185.85) * mm, "end": v(-304.59, 194.77) * mm});
            skLineSegment(sketch, "E387", {"start": v(-284.59, 183) * mm, "end": v(-284.59, 185) * mm});
            skLineSegment(sketch, "E388", {"start": v(-287.59, 190.08) * mm, "end": v(-287.59, 197.15) * mm});
            skLineSegment(sketch, "E389", {"start": v(-144.59, 152.33) * mm, "end": v(-144.59, 181) * mm});
            skLineSegment(sketch, "E390", {"start": v(-131.76, 195) * mm, "end": v(-131.76, 161) * mm});
            skLineSegment(sketch, "E391", {"start": v(-234.59, 185) * mm, "end": v(-234.59, 169.63) * mm});
            skLineSegment(sketch, "E392", {"start": v(-264.59, 181) * mm, "end": v(-264.59, 156.24) * mm});
            skLineSegment(sketch, "E393", {"start": v(-249.59, 183) * mm, "end": v(-249.59, 167) * mm});
            skLineSegment(sketch, "E394", {"start": v(-148.59, 178) * mm, "end": v(-148.59, 163) * mm});
            skArc(sketch, "E395", {"start": v(-209.59, 73) * mm, "mid": v(-181.79, 79.42) * mm, "end": v(-154.59, 88) * mm});
            skLineSegment(sketch, "E396", {"start": v(-249.59, 173.12) * mm, "end": v(-249.59, 140.24) * mm});
            skArc(sketch, "E397", {"start": v(-134.59, 93) * mm, "mid": v(-144.71, 91) * mm, "end": v(-154.59, 88) * mm});
            skLineSegment(sketch, "E398", {"start": v(-154.44, 100.97) * mm, "end": v(-151.18, 102.5) * mm});
            skLineSegment(sketch, "E399", {"start": v(-111.29, 72.28) * mm, "end": v(-111.29, 79.35) * mm});
            skLineSegment(sketch, "E400", {"start": v(-142.44, 100.97) * mm, "end": v(-145.7, 99.45) * mm});
            skCircle(sketch, "E401", {"center": v(-148.59, 173) * mm, "radius": 2 * mm});
            skLineSegment(sketch, "E402", {"start": v(-153.59, 173) * mm, "end": v(-128.76, 173) * mm});
            skLineSegment(sketch, "E403", {"start": v(-155.66, 156) * mm, "end": v(-160.59, 156) * mm});
            skCircle(sketch, "E404", {"center": v(-119.47, 136.3) * mm, "radius": 7 * mm});
            skLineSegment(sketch, "E405", {"start": v(-144.59, 156) * mm, "end": v(-148.59, 156) * mm});
            skLineSegment(sketch, "E406", {"start": v(-137.51, 156) * mm, "end": v(-132.59, 156) * mm});
            skLineSegment(sketch, "E407", {"start": v(-148.59, 174.12) * mm, "end": v(-148.59, 152.33) * mm});
            skCircle(sketch, "E408", {"center": v(-120.2, 164.62) * mm, "radius": 7 * mm});
            skLineSegment(sketch, "E409", {"start": v(-264.59, 185) * mm, "end": v(-244.59, 185) * mm});
            skLineSegment(sketch, "E410", {"start": v(-264.59, 185) * mm, "end": v(-264.59, 183) * mm});
            skLineSegment(sketch, "E411", {"start": v(-234.59, 192.08) * mm, "end": v(-234.59, 199.15) * mm});
            skLineSegment(sketch, "E412", {"start": v(-243.7, 185) * mm, "end": v(-232.82, 185) * mm});
            skLineSegment(sketch, "E413", {"start": v(-244.59, 183) * mm, "end": v(-244.59, 185) * mm});
            skLineSegment(sketch, "E414", {"start": v(-164.59, 185) * mm, "end": v(-144.59, 185) * mm});
            skLineSegment(sketch, "E415", {"start": v(-164.59, 185) * mm, "end": v(-164.59, 183) * mm});
            skLineSegment(sketch, "E416", {"start": v(-144.59, 187) * mm, "end": v(-144.59, 194.77) * mm});
            skLineSegment(sketch, "E417", {"start": v(-144.59, 183) * mm, "end": v(-144.59, 185) * mm});
            skArc(sketch, "E418", {"start": v(242.74, -102.75) * mm, "mid": v(225.17, -60.32) * mm, "end": v(182.74, -42.75) * mm});
            skLineSegment(sketch, "E419", {"start": v(211.47, 103.5) * mm, "end": v(401.47, 103.5) * mm});
            skLineSegment(sketch, "E420", {"start": v(211.47, 122.5) * mm, "end": v(401.47, 122.5) * mm});
            skLineSegment(sketch, "E421", {"start": v(185.42, 40.03) * mm, "end": v(241.76, 22.85) * mm});
            skLineSegment(sketch, "E422", {"start": v(184.37, 36.6) * mm, "end": v(241.76, 19.1) * mm});
            skLineSegment(sketch, "E423", {"start": v(182.74, -102.75) * mm, "end": v(225.17, -60.32) * mm});
            skLineSegment(sketch, "E424", {"start": v(211.47, 103) * mm, "end": v(221.47, 78) * mm});
            skLineSegment(sketch, "E425", {"start": v(209.23, 142.6) * mm, "end": v(240.37, 142.6) * mm});
            skLineSegment(sketch, "E426", {"start": v(211.47, 68) * mm, "end": v(221.47, 68) * mm});
            skLineSegment(sketch, "E427", {"start": v(222.42, 152.6) * mm, "end": v(211.53, 152.6) * mm});
            skLineSegment(sketch, "E428", {"start": v(222.42, 162.6) * mm, "end": v(211.53, 162.6) * mm});
            skLineSegment(sketch, "E429", {"start": v(201.47, 188) * mm, "end": v(341.47, 188) * mm});
            skLineSegment(sketch, "E430", {"start": v(201.47, 113) * mm, "end": v(401.47, 113) * mm});
            skLineSegment(sketch, "E431", {"start": v(208.54, 203) * mm, "end": v(394.4, 203) * mm});
            skLineSegment(sketch, "E432", {"start": v(208.54, 193) * mm, "end": v(326.47, 193) * mm});
            skLineSegment(sketch, "E433", {"start": v(2.74, -127.75) * mm, "end": v(235.67, -127.75) * mm});
            skLineSegment(sketch, "E434", {"start": v(165.41, 102.02) * mm, "end": v(165.41, 71.24) * mm});
            skLineSegment(sketch, "E435", {"start": v(211.47, 90.5) * mm, "end": v(211.47, 56.24) * mm});
            skLineSegment(sketch, "E436", {"start": v(60.41, 70) * mm, "end": v(60.41, 73) * mm});
            skLineSegment(sketch, "E437", {"start": v(-51.29, 66.1) * mm, "end": v(-51.29, 71.98) * mm});
            skLineSegment(sketch, "E438", {"start": v(-101.29, 52.21) * mm, "end": v(-101.29, 71.98) * mm});
            skLineSegment(sketch, "E439", {"start": v(95.76, -109.39) * mm, "end": v(36.03, -109.39) * mm});
            skLineSegment(sketch, "E440", {"start": v(95.76, -107.39) * mm, "end": v(34.91, -107.39) * mm});
            skLineSegment(sketch, "E441", {"start": v(48.52, -117.2) * mm, "end": v(59.85, -117.2) * mm});
            skLineSegment(sketch, "E442", {"start": v(22.16, -79.1) * mm, "end": v(70.91, -79.1) * mm});
            skLineSegment(sketch, "E443", {"start": v(2.74, -42.75) * mm, "end": v(182.74, -42.75) * mm});
            skLineSegment(sketch, "E444", {"start": v(-101.29, 50.21) * mm, "end": v(58.71, 50.21) * mm});
            skArc(sketch, "E445", {"start": v(58.71, 50.21) * mm, "mid": v(4.04, 60.08) * mm, "end": v(-51.29, 65.21) * mm});
            skLineSegment(sketch, "E446", {"start": v(-7.26, -39.75) * mm, "end": v(-7.26, -14.75) * mm});
            skArc(sketch, "E447", {"start": v(-79.38, -135.38) * mm, "mid": v(-69.92, -134.57) * mm, "end": v(-60.46, -133.63) * mm});
            skCircle(sketch, "E448", {"center": v(-69.53, -116.7) * mm, "radius": 7 * mm});
            skArc(sketch, "E449", {"start": v(-106.37, -133.08) * mm, "mid": v(-92.95, -135.14) * mm, "end": v(-79.38, -135.38) * mm});
            skLineSegment(sketch, "E450", {"start": v(-107.58, -124.27) * mm, "end": v(-107.58, -132) * mm});
            skLineSegment(sketch, "E451", {"start": v(-59.56, -124.27) * mm, "end": v(-59.56, -132) * mm});
            skLineSegment(sketch, "E452", {"start": v(5.7, -88.6) * mm, "end": v(22.16, -79.1) * mm});
            skArc(sketch, "E453", {"start": v(5.74, -92.75) * mm, "mid": v(4.94, -67.7) * mm, "end": v(2.74, -42.75) * mm});
            skLineSegment(sketch, "E454", {"start": v(2.74, -126.87) * mm, "end": v(2.74, -125.98) * mm});
            skLineSegment(sketch, "E455", {"start": v(32.05, -108.39) * mm, "end": v(23.05, -108.39) * mm});
            skFitSpline(sketch, "E456", {"points": [v(36.63, -105.53) * mm, v(35.63, -106.22) * mm, v(33.9, -107.6) * mm, v(36.94, -109.82) * mm, v(36.09, -111.07) * mm, v(35.65, -111.53) * mm]});
            skLineSegment(sketch, "E457", {"start": v(-7.26, -42.75) * mm, "end": v(-5.76, -42.75) * mm});
            skLineSegment(sketch, "E458", {"start": v(-8.76, -45.75) * mm, "end": v(-7.26, -45.75) * mm});
            skLineSegment(sketch, "E459", {"start": v(-28.23, 58.53) * mm, "end": v(-24.97, 60.05) * mm});
            skLineSegment(sketch, "E460", {"start": v(-16.23, 58.53) * mm, "end": v(-28.23, 58.53) * mm});
            skLineSegment(sketch, "E461", {"start": v(-94.22, 40.21) * mm, "end": v(51.64, 40.21) * mm});
            skArc(sketch, "E462", {"start": v(-51.29, 65.21) * mm, "mid": v(-77.6, 62.07) * mm, "end": v(-101.29, 50.21) * mm});
            skLineSegment(sketch, "E463", {"start": v(-94.22, 70.21) * mm, "end": v(-58.36, 70.21) * mm});
            skLineSegment(sketch, "E464", {"start": v(-65.3, 65.21) * mm, "end": v(-99.29, 65.21) * mm});
            skLineSegment(sketch, "E465", {"start": v(-101.29, 48.21) * mm, "end": v(-101.29, 38.44) * mm});
            skCircle(sketch, "E466", {"center": v(-41.87, 57.53) * mm, "radius": 7 * mm});
            skLineSegment(sketch, "E467", {"start": v(-16.23, 58.53) * mm, "end": v(-19.5, 57.01) * mm});
            skLineSegment(sketch, "E468", {"start": v(136.91, -9.08) * mm, "end": v(136.91, -36.56) * mm});
            skLineSegment(sketch, "E469", {"start": v(127.91, -3.15) * mm, "end": v(127.91, -35.1) * mm});
            skLineSegment(sketch, "E470", {"start": v(118.91, -9.08) * mm, "end": v(118.91, -34.5) * mm});
            skLineSegment(sketch, "E471", {"start": v(124.91, -13.28) * mm, "end": v(124.91, -34.38) * mm});
            skLineSegment(sketch, "E472", {"start": v(130.91, -13.28) * mm, "end": v(130.91, -37.3) * mm});
            skLineSegment(sketch, "E473", {"start": v(141.66, -76.89) * mm, "end": v(129.76, -88.79) * mm});
            skArc(sketch, "E474", {"start": v(129.76, -114.89) * mm, "mid": v(135.76, -120.89) * mm, "end": v(141.76, -114.89) * mm});
            skFitSpline(sketch, "E475", {"points": [v(115.77, -34.83) * mm, v(117.72, -34.62) * mm, v(121.2, -34.24) * mm, v(125.66, -34.27) * mm, v(128.98, -35.37) * mm, v(132.38, -39.41) * mm, v(136.46, -36.9) * mm, v(139.53, -35.02) * mm]});
            skLineSegment(sketch, "E476", {"start": v(135.76, -106.89) * mm, "end": v(115.76, -106.89) * mm});
            skLineSegment(sketch, "E477", {"start": v(106.73, -76.89) * mm, "end": v(135.66, -76.89) * mm});
            skLineSegment(sketch, "E478", {"start": v(123.66, -77.09) * mm, "end": v(135.86, -77.09) * mm});
            skLineSegment(sketch, "E479", {"start": v(123.66, -76.99) * mm, "end": v(135.76, -76.99) * mm});
            skLineSegment(sketch, "E480", {"start": v(116.66, -70.69) * mm, "end": v(154.66, -70.69) * mm});
            skLineSegment(sketch, "E481", {"start": v(116.66, -70.79) * mm, "end": v(154.66, -70.79) * mm});
            skLineSegment(sketch, "E482", {"start": v(104.36, -70.89) * mm, "end": v(166.02, -70.89) * mm});
            skLineSegment(sketch, "E483", {"start": v(105.76, -106.89) * mm, "end": v(65.76, -106.89) * mm});
            skLineSegment(sketch, "E484", {"start": v(80.68, -96.89) * mm, "end": v(129.76, -96.89) * mm});
            skLineSegment(sketch, "E485", {"start": v(59.85, -117.2) * mm, "end": v(66.24, -109.39) * mm});
            skLineSegment(sketch, "E486", {"start": v(71.31, -106.39) * mm, "end": v(69.86, -110.39) * mm});
            skLineSegment(sketch, "E487", {"start": v(73.44, -106.39) * mm, "end": v(71.99, -110.39) * mm});
            skLineSegment(sketch, "E488", {"start": v(92.6, -106.39) * mm, "end": v(91.14, -110.39) * mm});
            skLineSegment(sketch, "E489", {"start": v(90.47, -106.39) * mm, "end": v(89.01, -110.39) * mm});
            skLineSegment(sketch, "E490", {"start": v(86.21, -106.39) * mm, "end": v(84.76, -110.39) * mm});
            skLineSegment(sketch, "E491", {"start": v(88.34, -106.39) * mm, "end": v(86.89, -110.39) * mm});
            skLineSegment(sketch, "E492", {"start": v(79.83, -106.39) * mm, "end": v(78.37, -110.39) * mm});
            skLineSegment(sketch, "E493", {"start": v(77.7, -106.39) * mm, "end": v(76.24, -110.39) * mm});
            skLineSegment(sketch, "E494", {"start": v(81.96, -106.39) * mm, "end": v(80.5, -110.39) * mm});
            skLineSegment(sketch, "E495", {"start": v(84.09, -106.39) * mm, "end": v(82.63, -110.39) * mm});
            skLineSegment(sketch, "E496", {"start": v(75.57, -106.39) * mm, "end": v(74.12, -110.39) * mm});
            skLineSegment(sketch, "E497", {"start": v(129.76, -88.79) * mm, "end": v(129.76, -114.89) * mm});
            skLineSegment(sketch, "E498", {"start": v(110.76, -116.89) * mm, "end": v(105.76, -106.89) * mm});
            skLineSegment(sketch, "E499", {"start": v(115.76, -106.89) * mm, "end": v(110.76, -116.89) * mm});
            skLineSegment(sketch, "E500", {"start": v(95.76, -107.39) * mm, "end": v(95.76, -109.39) * mm});
            skLineSegment(sketch, "E501", {"start": v(92.3, -66.62) * mm, "end": v(111.33, -66.62) * mm});
            skLineSegment(sketch, "E502", {"start": v(111.33, -66.62) * mm, "end": v(115.5, -71.72) * mm});
            skLineSegment(sketch, "E503", {"start": v(94.3, -86.04) * mm, "end": v(122.77, -86.04) * mm});
            skFitSpline(sketch, "E504", {"points": [v(107.4, -68.18) * mm, v(105.42, -69.54) * mm, v(101.96, -72.3) * mm, v(108.03, -76.74) * mm, v(106.32, -79.25) * mm, v(105.46, -80.18) * mm]});
            skLineSegment(sketch, "E505", {"start": v(122.77, -86.04) * mm, "end": v(130.08, -77.09) * mm});
            skLineSegment(sketch, "E506", {"start": v(155.76, -76.89) * mm, "end": v(141.76, -90.89) * mm});
            skLineSegment(sketch, "E507", {"start": v(141.76, -90.89) * mm, "end": v(141.76, -114.89) * mm});
            skCircle(sketch, "E508", {"center": v(135.76, -114.89) * mm, "radius": 0.8 * mm});
            skCircle(sketch, "E509", {"center": v(135.76, -98.89) * mm, "radius": 0.8 * mm});
            skCircle(sketch, "E510", {"center": v(135.76, -106.89) * mm, "radius": 0.8 * mm});
            skLineSegment(sketch, "E511", {"start": v(185.24, -102.75) * mm, "end": v(180.24, -102.75) * mm});
            skLineSegment(sketch, "E512", {"start": v(182.74, -100.25) * mm, "end": v(182.74, -105.25) * mm});
            skLineSegment(sketch, "E513", {"start": v(162.28, -66.62) * mm, "end": v(185.99, -66.62) * mm});
            skLineSegment(sketch, "E514", {"start": v(147.7, -60.37) * mm, "end": v(175.98, -60.37) * mm});
            skLineSegment(sketch, "E515", {"start": v(147.7, -60.37) * mm, "end": v(139.27, -70.69) * mm});
            skLineSegment(sketch, "E516", {"start": v(141.66, -76.89) * mm, "end": v(163.64, -76.89) * mm});
            skLineSegment(sketch, "E517", {"start": v(141.58, -77.09) * mm, "end": v(153.66, -77.09) * mm});
            skLineSegment(sketch, "E518", {"start": v(141.62, -76.99) * mm, "end": v(153.66, -76.99) * mm});
            skLineSegment(sketch, "E519", {"start": v(135.66, -70.89) * mm, "end": v(141.66, -76.89) * mm});
            skLineSegment(sketch, "E520", {"start": v(135.66, -70.89) * mm, "end": v(135.66, -76.89) * mm});
            skLineSegment(sketch, "E521", {"start": v(135.86, -71.37) * mm, "end": v(141.58, -77.09) * mm});
            skLineSegment(sketch, "E522", {"start": v(135.86, -71.37) * mm, "end": v(135.86, -77.09) * mm});
            skLineSegment(sketch, "E523", {"start": v(135.76, -71.13) * mm, "end": v(135.76, -76.99) * mm});
            skLineSegment(sketch, "E524", {"start": v(135.76, -71.13) * mm, "end": v(141.62, -76.99) * mm});
            skLineSegment(sketch, "E525", {"start": v(162.28, -66.62) * mm, "end": v(158.1, -71.72) * mm});
            skFitSpline(sketch, "E526", {"points": [v(162.97, -68.18) * mm, v(164.96, -69.54) * mm, v(168.41, -72.3) * mm, v(162.34, -76.74) * mm, v(164.05, -79.25) * mm, v(164.92, -80.18) * mm]});
            skLineSegment(sketch, "E527", {"start": v(155.76, -70.89) * mm, "end": v(155.76, -76.89) * mm});
            skLineSegment(sketch, "E528", {"start": v(129.7, -22.82) * mm, "end": v(146.7, -10.92) * mm});
            skLineSegment(sketch, "E529", {"start": v(145.91, -26.68) * mm, "end": v(109.91, -26.68) * mm});
            skLineSegment(sketch, "E530", {"start": v(132.5, -14.61) * mm, "end": v(137.16, -21.27) * mm});
            skLineSegment(sketch, "E531", {"start": v(152.75, 2) * mm, "end": v(130.91, -13.28) * mm});
            skLineSegment(sketch, "E532", {"start": v(136.91, -9.08) * mm, "end": v(128.63, -9.08) * mm});
            skLineSegment(sketch, "E533", {"start": v(150.33, 7.64) * mm, "end": v(127.91, -8.06) * mm});
            skLineSegment(sketch, "E534", {"start": v(158.34, 33.66) * mm, "end": v(97.49, 33.66) * mm});
            skLineSegment(sketch, "E535", {"start": v(90.41, 43.66) * mm, "end": v(90.41, -5.34) * mm});
            skLineSegment(sketch, "E536", {"start": v(103.08, 2) * mm, "end": v(124.91, -13.28) * mm});
            skLineSegment(sketch, "E537", {"start": v(104.97, -2.08) * mm, "end": v(104.97, -19.34) * mm});
            skLineSegment(sketch, "E538", {"start": v(105.5, 7.64) * mm, "end": v(127.91, -8.06) * mm});
            skLineSegment(sketch, "E539", {"start": v(115.97, -9.08) * mm, "end": v(102.97, -9.08) * mm});
            skLineSegment(sketch, "E540", {"start": v(117.8, -10.74) * mm, "end": v(113.14, -17.4) * mm});
            skLineSegment(sketch, "E541", {"start": v(126.12, -22.82) * mm, "end": v(109.13, -10.92) * mm});
            skLineSegment(sketch, "E542", {"start": v(108.97, -12.34) * mm, "end": v(102.97, -12.34) * mm});
            skLineSegment(sketch, "E543", {"start": v(130.91, -13.28) * mm, "end": v(130.91, -12.34) * mm});
            skLineSegment(sketch, "E544", {"start": v(124.91, -13.28) * mm, "end": v(124.91, -12.34) * mm});
            skLineSegment(sketch, "E545", {"start": v(127.2, -9.08) * mm, "end": v(128.63, -9.08) * mm});
            skLineSegment(sketch, "E546", {"start": v(127.2, -9.08) * mm, "end": v(118.91, -9.08) * mm});
            skLineSegment(sketch, "E547", {"start": v(127.91, -8.06) * mm, "end": v(131.36, -12.97) * mm});
            skLineSegment(sketch, "E548", {"start": v(124.47, -12.97) * mm, "end": v(127.91, -8.06) * mm});
            skLineSegment(sketch, "E549", {"start": v(123.33, -14.61) * mm, "end": v(118.67, -21.27) * mm});
            skFitSpline(sketch, "E550", {"points": [v(101.25, 1.51) * mm, v(101.74, 1.65) * mm, v(102.88, 1.95) * mm, v(104.8, 2.45) * mm, v(105.03, 4.6) * mm, v(103.63, 6.27) * mm, v(105.12, 7.45) * mm, v(106.22, 8.04) * mm, v(106.91, 8.44) * mm, v(107.3, 8.66) * mm]});
            skLineSegment(sketch, "E551", {"start": v(122.2, -2.15) * mm, "end": v(133.63, -2.15) * mm});
            skLineSegment(sketch, "E552", {"start": v(128.63, -6.15) * mm, "end": v(128.63, -0.15) * mm});
            skLineSegment(sketch, "E553", {"start": v(127.2, -6.15) * mm, "end": v(127.2, -0.15) * mm});
            skArc(sketch, "E554", {"start": v(134.48, 4.92) * mm, "mid": v(127.91, 6.48) * mm, "end": v(121.35, 4.92) * mm});
            skLineSegment(sketch, "E555", {"start": v(58.71, 48.21) * mm, "end": v(58.71, 38.44) * mm});
            skLineSegment(sketch, "E556", {"start": v(165.41, 23.66) * mm, "end": v(165.41, 14.66) * mm});
            skLineSegment(sketch, "E557", {"start": v(174.27, 37.8) * mm, "end": v(174.27, 0.52) * mm});
            skLineSegment(sketch, "E558", {"start": v(178.3, 14.66) * mm, "end": v(170.24, 14.66) * mm});
            skLineSegment(sketch, "E559", {"start": v(150.86, -2.08) * mm, "end": v(150.86, -20.28) * mm});
            skLineSegment(sketch, "E560", {"start": v(145.86, -13.28) * mm, "end": v(152.86, -13.28) * mm});
            skLineSegment(sketch, "E561", {"start": v(139.86, -9.08) * mm, "end": v(152.86, -9.08) * mm});
            skLineSegment(sketch, "E562", {"start": v(138.03, -10.74) * mm, "end": v(142.69, -17.4) * mm});
            skFitSpline(sketch, "E563", {"points": [v(154.58, 1.51) * mm, v(154.09, 1.65) * mm, v(152.95, 1.95) * mm, v(151.03, 2.45) * mm, v(150.8, 4.6) * mm, v(152.2, 6.27) * mm, v(150.7, 7.45) * mm, v(149.6, 8.04) * mm, v(148.92, 8.44) * mm, v(148.54, 8.66) * mm]});
            skLineSegment(sketch, "E564", {"start": v(165.41, 14.66) * mm, "end": v(165.41, -5.34) * mm});
            skLineSegment(sketch, "E565", {"start": v(178.3, 23.66) * mm, "end": v(170.24, 23.66) * mm});
            skLineSegment(sketch, "E566", {"start": v(165.41, 23.66) * mm, "end": v(165.41, 43.66) * mm});
            skLineSegment(sketch, "E567", {"start": v(184.37, 36.6) * mm, "end": v(185.42, 40.03) * mm});
            skLineSegment(sketch, "E568", {"start": v(204.4, 68) * mm, "end": v(197.33, 68) * mm});
            skArc(sketch, "E569", {"start": v(0.37, 142.14) * mm, "mid": v(44.84, 131.56) * mm, "end": v(90.41, 128) * mm});
            skArc(sketch, "E570", {"start": v(-4.59, 93) * mm, "mid": v(35.3, 88.68) * mm, "end": v(75.41, 88) * mm});
            skLineSegment(sketch, "E571", {"start": v(-74.59, 95) * mm, "end": v(-74.59, 83.54) * mm});
            skArc(sketch, "E572", {"start": v(0.37, 142.14) * mm, "mid": v(-9.82, 146.64) * mm, "end": v(-20.12, 150.85) * mm});
            skLineSegment(sketch, "E573", {"start": v(-73.7, 183) * mm, "end": v(-2.82, 183) * mm});
            skLineSegment(sketch, "E574", {"start": v(204.87, 188) * mm, "end": v(204.87, 113) * mm});
            skLineSegment(sketch, "E575", {"start": v(181.47, 188) * mm, "end": v(181.47, 78) * mm});
            skLineSegment(sketch, "E576", {"start": v(201.47, 188) * mm, "end": v(201.47, 113) * mm});
            skLineSegment(sketch, "E577", {"start": v(165.41, 131) * mm, "end": v(165.41, 206) * mm});
            skLineSegment(sketch, "E578", {"start": v(191.47, 180.94) * mm, "end": v(191.47, 120.08) * mm});
            skLineSegment(sketch, "E579", {"start": v(90.41, 125.9) * mm, "end": v(165.41, 125.9) * mm});
            skLineSegment(sketch, "E580", {"start": v(90.41, 128) * mm, "end": v(165.41, 128) * mm});
            skArc(sketch, "E581", {"start": v(75.41, 88) * mm, "mid": v(112.96, 89.8) * mm, "end": v(150.41, 93) * mm});
            skLineSegment(sketch, "E582", {"start": v(90.41, 128) * mm, "end": v(90.41, 125.9) * mm});
            skLineSegment(sketch, "E583", {"start": v(200.41, 128) * mm, "end": v(200.41, 108) * mm});
            skLineSegment(sketch, "E584", {"start": v(165.41, 128) * mm, "end": v(165.41, 108) * mm});
            skArc(sketch, "E585", {"start": v(150.41, 93) * mm, "mid": v(160.57, 97.85) * mm, "end": v(165.41, 108) * mm});
            skLineSegment(sketch, "E586", {"start": v(191.47, 105.94) * mm, "end": v(191.47, 78) * mm});
            skLineSegment(sketch, "E587", {"start": v(209.47, 78) * mm, "end": v(178.47, 78) * mm});
            skLineSegment(sketch, "E588", {"start": v(209.47, 78) * mm, "end": v(197.7, 78) * mm});
            skLineSegment(sketch, "E589", {"start": v(199.47, 113) * mm, "end": v(189.7, 113) * mm});
            skLineSegment(sketch, "E590", {"start": v(211.47, 113) * mm, "end": v(211.47, 122.5) * mm});
            skLineSegment(sketch, "E591", {"start": v(211.47, 113) * mm, "end": v(211.47, 103) * mm});
            skLineSegment(sketch, "E592", {"start": v(145.8, 141) * mm, "end": v(145.8, 135.08) * mm});
            skLineSegment(sketch, "E593", {"start": v(192.47, 127.6) * mm, "end": v(213.87, 127.6) * mm});
            skLineSegment(sketch, "E594", {"start": v(213.3, 145.53) * mm, "end": v(213.3, 138.46) * mm});
            skLineSegment(sketch, "E595", {"start": v(213.3, 162.6) * mm, "end": v(213.3, 152.6) * mm});
            skLineSegment(sketch, "E596", {"start": v(213.3, 169.67) * mm, "end": v(213.3, 176.74) * mm});
            skLineSegment(sketch, "E597", {"start": v(201.47, 190) * mm, "end": v(201.47, 204.77) * mm});
            skLineSegment(sketch, "E598", {"start": v(199.47, 188) * mm, "end": v(178.47, 188) * mm});
            skLineSegment(sketch, "E599", {"start": v(201.47, 190) * mm, "end": v(201.47, 194.77) * mm});
            skLineSegment(sketch, "E600", {"start": v(221.47, 76) * mm, "end": v(221.47, 66.24) * mm});
            skLineSegment(sketch, "E601", {"start": v(401.47, 72.12) * mm, "end": v(401.47, 56.24) * mm});
            skLineSegment(sketch, "E602", {"start": v(382.77, -73.7) * mm, "end": v(346.46, -73.7) * mm});
            skLineSegment(sketch, "E603", {"start": v(279.46, -45.2) * mm, "end": v(379.46, -45.2) * mm});
            skLineSegment(sketch, "E604", {"start": v(376.96, -63.7) * mm, "end": v(393.27, -63.7) * mm});
            skLineSegment(sketch, "E605", {"start": v(364.4, -55.2) * mm, "end": v(389.53, -55.2) * mm});
            skLineSegment(sketch, "E606", {"start": v(374.46, -66.7) * mm, "end": v(379.46, -66.7) * mm});
            skLineSegment(sketch, "E607", {"start": v(344.26, 19.1) * mm, "end": v(399.15, 19.1) * mm});
            skLineSegment(sketch, "E608", {"start": v(399.15, 36.6) * mm, "end": v(341.76, 19.1) * mm});
            skLineSegment(sketch, "E609", {"start": v(398.1, 40.03) * mm, "end": v(341.76, 22.85) * mm});
            skLineSegment(sketch, "E610", {"start": v(228.54, 68) * mm, "end": v(401.47, 68) * mm});
            skLineSegment(sketch, "E611", {"start": v(394.4, 58) * mm, "end": v(218.54, 58) * mm});
            skLineSegment(sketch, "E612", {"start": v(316.46, -77.93) * mm, "end": v(276.46, -77.93) * mm});
            skLineSegment(sketch, "E613", {"start": v(294.46, -63.7) * mm, "end": v(314.46, -63.7) * mm});
            skLineSegment(sketch, "E614", {"start": v(217.74, -42.75) * mm, "end": v(257.74, -42.75) * mm});
            skLineSegment(sketch, "E615", {"start": v(274.46, -81.77) * mm, "end": v(274.46, -52.47) * mm});
            skLineSegment(sketch, "E616", {"start": v(268.46, -63.7) * mm, "end": v(277.46, -63.7) * mm});
            skLineSegment(sketch, "E617", {"start": v(268.46, -70.7) * mm, "end": v(277.46, -70.7) * mm});
            skLineSegment(sketch, "E618", {"start": v(279.46, -63.7) * mm, "end": v(279.46, -70.7) * mm});
            skLineSegment(sketch, "E619", {"start": v(291.96, -68.7) * mm, "end": v(294.46, -63.7) * mm});
            skLineSegment(sketch, "E620", {"start": v(289.46, -63.7) * mm, "end": v(291.96, -68.7) * mm});
            skLineSegment(sketch, "E621", {"start": v(279.46, -72.98) * mm, "end": v(279.46, -80.93) * mm});
            skLineSegment(sketch, "E622", {"start": v(279.46, -63.7) * mm, "end": v(289.46, -63.7) * mm});
            skLineSegment(sketch, "E623", {"start": v(279.46, -60.31) * mm, "end": v(279.46, -43.43) * mm});
            skLineSegment(sketch, "E624", {"start": v(334.61, -62.2) * mm, "end": v(364.46, -62.2) * mm});
            skLineSegment(sketch, "E625", {"start": v(335.33, -63.2) * mm, "end": v(364.46, -63.2) * mm});
            skFitSpline(sketch, "E626", {"points": [v(336.19, -59.7) * mm, v(335.2, -60.38) * mm, v(333.46, -61.76) * mm, v(336.5, -63.98) * mm, v(335.64, -65.24) * mm, v(335.2, -65.7) * mm]});
            skFitSpline(sketch, "E627", {"points": [v(331.1, -59.7) * mm, v(330.1, -60.38) * mm, v(328.38, -61.76) * mm, v(331.41, -63.98) * mm, v(330.56, -65.24) * mm, v(330.12, -65.7) * mm]});
            skLineSegment(sketch, "E628", {"start": v(299.46, -62.2) * mm, "end": v(329.53, -62.2) * mm});
            skLineSegment(sketch, "E629", {"start": v(299.46, -63.2) * mm, "end": v(330.24, -63.2) * mm});
            skLineSegment(sketch, "E630", {"start": v(299.46, -72.93) * mm, "end": v(299.46, -80.93) * mm});
            skLineSegment(sketch, "E631", {"start": v(314.46, -72.93) * mm, "end": v(314.46, -80.93) * mm});
            skLineSegment(sketch, "E632", {"start": v(309.65, -64.2) * mm, "end": v(310.74, -61.2) * mm});
            skLineSegment(sketch, "E633", {"start": v(310.71, -64.2) * mm, "end": v(311.8, -61.2) * mm});
            skLineSegment(sketch, "E634", {"start": v(311.78, -64.2) * mm, "end": v(312.87, -61.2) * mm});
            skLineSegment(sketch, "E635", {"start": v(305.4, -64.2) * mm, "end": v(306.49, -61.2) * mm});
            skLineSegment(sketch, "E636", {"start": v(306.46, -64.2) * mm, "end": v(307.55, -61.2) * mm});
            skLineSegment(sketch, "E637", {"start": v(308.59, -64.2) * mm, "end": v(309.68, -61.2) * mm});
            skLineSegment(sketch, "E638", {"start": v(307.52, -64.2) * mm, "end": v(308.61, -61.2) * mm});
            skLineSegment(sketch, "E639", {"start": v(303.27, -64.2) * mm, "end": v(304.36, -61.2) * mm});
            skLineSegment(sketch, "E640", {"start": v(304.33, -64.2) * mm, "end": v(305.42, -61.2) * mm});
            skLineSegment(sketch, "E641", {"start": v(302.2, -64.2) * mm, "end": v(303.3, -61.2) * mm});
            skLineSegment(sketch, "E642", {"start": v(301.14, -64.2) * mm, "end": v(302.23, -61.2) * mm});
            skLineSegment(sketch, "E643", {"start": v(299.46, -63.2) * mm, "end": v(299.46, -62.2) * mm});
            skLineSegment(sketch, "E644", {"start": v(358.53, -64.2) * mm, "end": v(357.44, -61.2) * mm});
            skLineSegment(sketch, "E645", {"start": v(349.46, -63.7) * mm, "end": v(374.46, -63.7) * mm});
            skLineSegment(sketch, "E646", {"start": v(349.46, -65.7) * mm, "end": v(349.46, -78.7) * mm});
            skLineSegment(sketch, "E647", {"start": v(356.4, -64.2) * mm, "end": v(355.31, -61.2) * mm});
            skLineSegment(sketch, "E648", {"start": v(355.34, -64.2) * mm, "end": v(354.25, -61.2) * mm});
            skLineSegment(sketch, "E649", {"start": v(357.47, -64.2) * mm, "end": v(356.38, -61.2) * mm});
            skLineSegment(sketch, "E650", {"start": v(352.15, -64.2) * mm, "end": v(351.06, -61.2) * mm});
            skLineSegment(sketch, "E651", {"start": v(353.21, -64.2) * mm, "end": v(352.12, -61.2) * mm});
            skLineSegment(sketch, "E652", {"start": v(354.28, -64.2) * mm, "end": v(353.19, -61.2) * mm});
            skLineSegment(sketch, "E653", {"start": v(374.46, -68.7) * mm, "end": v(374.46, -78.7) * mm});
            skLineSegment(sketch, "E654", {"start": v(364.46, -65.7) * mm, "end": v(364.46, -78.7) * mm});
            skLineSegment(sketch, "E655", {"start": v(362.8, -64.2) * mm, "end": v(361.7, -61.2) * mm});
            skLineSegment(sketch, "E656", {"start": v(361.73, -64.2) * mm, "end": v(360.63, -61.2) * mm});
            skLineSegment(sketch, "E657", {"start": v(359.6, -64.2) * mm, "end": v(358.5, -61.2) * mm});
            skLineSegment(sketch, "E658", {"start": v(360.66, -64.2) * mm, "end": v(359.57, -61.2) * mm});
            skLineSegment(sketch, "E659", {"start": v(364.46, -63.2) * mm, "end": v(364.46, -62.2) * mm});
            skLineSegment(sketch, "E660", {"start": v(374.46, -63.7) * mm, "end": v(374.46, -66.7) * mm});
            skLineSegment(sketch, "E661", {"start": v(374.46, -60.31) * mm, "end": v(374.46, -53.43) * mm});
            skCircle(sketch, "E662", {"center": v(291.76, 7.08) * mm, "radius": 15.88 * mm});
            skArc(sketch, "E663", {"start": v(321.12, 33.22) * mm, "mid": v(291.76, 45.44) * mm, "end": v(262.4, 33.22) * mm});
            skLineSegment(sketch, "E664", {"start": v(295.86, 6.02) * mm, "end": v(298.3, 2.54) * mm});
            skLineSegment(sketch, "E665", {"start": v(296.06, 6.16) * mm, "end": v(298.5, 2.68) * mm});
            skLineSegment(sketch, "E666", {"start": v(313.24, 19.1) * mm, "end": v(292.89, 4.85) * mm});
            skLineSegment(sketch, "E667", {"start": v(314.55, 19.1) * mm, "end": v(292.89, 3.94) * mm});
            skLineSegment(sketch, "E668", {"start": v(241.76, 22.85) * mm, "end": v(341.76, 22.85) * mm});
            skLineSegment(sketch, "E669", {"start": v(241.76, 19.1) * mm, "end": v(341.76, 19.1) * mm});
            skLineSegment(sketch, "E670", {"start": v(295.51, 19.1) * mm, "end": v(295.51, 18.6) * mm});
            skLineSegment(sketch, "E671", {"start": v(288.01, 19.1) * mm, "end": v(288.01, 18.6) * mm});
            skLineSegment(sketch, "E672", {"start": v(270.29, 19.1) * mm, "end": v(290.64, 4.85) * mm});
            skLineSegment(sketch, "E673", {"start": v(268.98, 19.1) * mm, "end": v(290.64, 3.94) * mm});
            skLineSegment(sketch, "E674", {"start": v(291.76, 24.35) * mm, "end": v(291.76, -12.9) * mm});
            skLineSegment(sketch, "E675", {"start": v(290.64, 18.6) * mm, "end": v(290.64, -11.4) * mm});
            skLineSegment(sketch, "E676", {"start": v(292.89, 18.6) * mm, "end": v(292.89, -11.4) * mm});
            skLineSegment(sketch, "E677", {"start": v(290.64, -11.4) * mm, "end": v(292.89, -11.4) * mm});
            skLineSegment(sketch, "E678", {"start": v(288.01, 18.6) * mm, "end": v(295.51, 18.6) * mm});
            skLineSegment(sketch, "E679", {"start": v(295.51, 16.6) * mm, "end": v(295.51, 15.6) * mm});
            skLineSegment(sketch, "E680", {"start": v(292.89, 16.6) * mm, "end": v(295.51, 16.6) * mm});
            skLineSegment(sketch, "E681", {"start": v(292.89, 15.6) * mm, "end": v(295.51, 15.6) * mm});
            skLineSegment(sketch, "E682", {"start": v(288.01, 16.6) * mm, "end": v(290.64, 16.6) * mm});
            skLineSegment(sketch, "E683", {"start": v(288.01, 15.6) * mm, "end": v(290.64, 15.6) * mm});
            skLineSegment(sketch, "E684", {"start": v(288.01, 16.6) * mm, "end": v(288.01, 15.6) * mm});
            skLineSegment(sketch, "E685", {"start": v(285.02, 2.68) * mm, "end": v(285.23, 2.54) * mm});
            skLineSegment(sketch, "E686", {"start": v(287.46, 6.16) * mm, "end": v(285.02, 2.68) * mm});
            skLineSegment(sketch, "E687", {"start": v(287.67, 6.02) * mm, "end": v(285.23, 2.54) * mm});
            skLineSegment(sketch, "E688", {"start": v(250.8, 32.74) * mm, "end": v(264.93, 22.85) * mm});
            skLineSegment(sketch, "E689", {"start": v(250.37, 32.13) * mm, "end": v(263.62, 22.85) * mm});
            skLineSegment(sketch, "E690", {"start": v(250.8, 32.74) * mm, "end": v(250.37, 32.13) * mm});
            skLineSegment(sketch, "E691", {"start": v(241.76, 22.85) * mm, "end": v(241.76, 19.1) * mm});
            skLineSegment(sketch, "E692", {"start": v(298.5, 2.68) * mm, "end": v(298.3, 2.54) * mm});
            skLineSegment(sketch, "E693", {"start": v(332.72, 32.74) * mm, "end": v(333.15, 32.13) * mm});
            skLineSegment(sketch, "E694", {"start": v(333.15, 32.13) * mm, "end": v(319.9, 22.85) * mm});
            skLineSegment(sketch, "E695", {"start": v(332.72, 32.74) * mm, "end": v(318.6, 22.85) * mm});
            skLineSegment(sketch, "E696", {"start": v(341.76, 22.85) * mm, "end": v(341.76, 19.1) * mm});
            skCircle(sketch, "E697", {"center": v(390.65, -40.95) * mm, "radius": 7 * mm});
            skLineSegment(sketch, "E698", {"start": v(391.5, -79.77) * mm, "end": v(391.5, -54.7) * mm});
            skLineSegment(sketch, "E699", {"start": v(381.46, -66.7) * mm, "end": v(393.27, -66.7) * mm});
            skLineSegment(sketch, "E700", {"start": v(379.46, -60.31) * mm, "end": v(379.46, -43.43) * mm});
            skLineSegment(sketch, "E701", {"start": v(399.15, 36.6) * mm, "end": v(398.1, 40.03) * mm});
            skLineSegment(sketch, "E702", {"start": v(399.15, 36.6) * mm, "end": v(399.15, 19.1) * mm});
            skLineSegment(sketch, "E703", {"start": v(341.47, 128) * mm, "end": v(383.9, 170.43) * mm});
            skArc(sketch, "E704", {"start": v(401.47, 128) * mm, "mid": v(383.9, 170.43) * mm, "end": v(341.47, 188) * mm});
            skLineSegment(sketch, "E705", {"start": v(221.47, 78) * mm, "end": v(401.47, 78) * mm});
            skCircle(sketch, "E706", {"center": v(373.95, 130.45) * mm, "radius": 7 * mm});
            skLineSegment(sketch, "E707", {"start": v(248.3, 168.01) * mm, "end": v(248.3, 179.37) * mm});
            skLineSegment(sketch, "E708", {"start": v(223.3, 163.49) * mm, "end": v(223.3, 179.37) * mm});
            skLineSegment(sketch, "E709", {"start": v(222.47, 103) * mm, "end": v(222.47, 113) * mm});
            skLineSegment(sketch, "E710", {"start": v(221.47, 103) * mm, "end": v(222.47, 103) * mm});
            skLineSegment(sketch, "E711", {"start": v(221.47, 113) * mm, "end": v(221.47, 103) * mm});
            skLineSegment(sketch, "E712", {"start": v(254.37, 175.6) * mm, "end": v(254.37, 149.6) * mm});
            skLineSegment(sketch, "E713", {"start": v(226.3, 151.72) * mm, "end": v(226.3, 140.83) * mm});
            skLineSegment(sketch, "E714", {"start": v(223.3, 151.72) * mm, "end": v(223.3, 140.83) * mm});
            skCircle(sketch, "E715", {"center": v(248.34, 141.58) * mm, "radius": 7 * mm});
            skLineSegment(sketch, "E716", {"start": v(235.8, 162.6) * mm, "end": v(238.8, 162.6) * mm});
            skLineSegment(sketch, "E717", {"start": v(232.25, 165.6) * mm, "end": v(245.3, 165.6) * mm});
            skLineSegment(sketch, "E718", {"start": v(233.3, 159.6) * mm, "end": v(245.3, 159.6) * mm});
            skLineSegment(sketch, "E719", {"start": v(230.37, 177.6) * mm, "end": v(248.3, 177.6) * mm});
            skLineSegment(sketch, "E720", {"start": v(226.3, 159.65) * mm, "end": v(232.25, 165.6) * mm});
            skLineSegment(sketch, "E721", {"start": v(223.3, 162.65) * mm, "end": v(226.3, 159.65) * mm});
            skLineSegment(sketch, "E722", {"start": v(223.3, 152.6) * mm, "end": v(226.3, 152.6) * mm});
            skLineSegment(sketch, "E723", {"start": v(226.3, 152.6) * mm, "end": v(233.3, 159.6) * mm});
            skLineSegment(sketch, "E724", {"start": v(223.3, 162.65) * mm, "end": v(223.3, 152.6) * mm});
            skArc(sketch, "E725", {"start": v(245.3, 159.6) * mm, "mid": v(248.3, 162.6) * mm, "end": v(245.3, 165.6) * mm});
            skCircle(sketch, "E726", {"center": v(245.3, 162.6) * mm, "radius": 0.4 * mm});
            skLineSegment(sketch, "E727", {"start": v(243.8, 162.6) * mm, "end": v(246.8, 162.6) * mm});
            skLineSegment(sketch, "E728", {"start": v(245.3, 164.1) * mm, "end": v(245.3, 161.1) * mm});
            skLineSegment(sketch, "E729", {"start": v(249.37, 165.6) * mm, "end": v(256.37, 165.6) * mm});
            skLineSegment(sketch, "E730", {"start": v(249.37, 159.6) * mm, "end": v(256.37, 159.6) * mm});
            skLineSegment(sketch, "E731", {"start": v(241.3, 164.1) * mm, "end": v(241.3, 161.1) * mm});
            skCircle(sketch, "E732", {"center": v(237.3, 162.6) * mm, "radius": 0.4 * mm});
            skLineSegment(sketch, "E733", {"start": v(237.3, 164.1) * mm, "end": v(237.3, 161.1) * mm});
            skLineSegment(sketch, "E734", {"start": v(239.8, 162.6) * mm, "end": v(242.8, 162.6) * mm});
            skCircle(sketch, "E735", {"center": v(241.3, 162.6) * mm, "radius": 0.4 * mm});
            skCircle(sketch, "E736", {"center": v(316.65, 94.53) * mm, "radius": 7 * mm});
            skLineSegment(sketch, "E737", {"start": v(318.46, 144.5) * mm, "end": v(315.2, 142.99) * mm});
            skLineSegment(sketch, "E738", {"start": v(318.46, 144.5) * mm, "end": v(306.46, 144.5) * mm});
            skLineSegment(sketch, "E739", {"start": v(306.46, 144.5) * mm, "end": v(309.72, 146.03) * mm});
            skCircle(sketch, "E740", {"center": v(311.83, 163.53) * mm, "radius": 7 * mm});
            skLineSegment(sketch, "E741", {"start": v(341.47, 130.5) * mm, "end": v(341.47, 125.5) * mm});
            skLineSegment(sketch, "E742", {"start": v(343.97, 128) * mm, "end": v(338.97, 128) * mm});
            skLineSegment(sketch, "E743", {"start": v(326.47, 190) * mm, "end": v(326.47, 198) * mm});
            skLineSegment(sketch, "E744", {"start": v(401.47, 173.36) * mm, "end": v(401.47, 204.77) * mm});
            skLineSegment(sketch, "E745", {"start": v(401.47, 128) * mm, "end": v(401.47, 78) * mm});
            skLineSegment(sketch, "E746", {"start": v(407.74, 74.25) * mm, "end": v(412.74, 74.25) * mm});
            skLineSegment(sketch, "E747.trimOffspring", {"start": v(60.41, 128) * mm, "end": v(60.41, 129.54) * mm});
            skSolve(sketch);
        }
        {
            var Q0;
            Q0=makeQuery(id+"F0.imprint","IMPRINT",FACE,{"disambiguationData":[TD([[makeQuery(id+"F0.imprint","IMPRINT",EDGE,{"derivedFrom":sQuery(id+"F0.wireOp",EDGE,"E370")}),-1.0]])]});
            var Q1;
            {var subQ0=sQuery(id+"F0.wireOp",EDGE,"E335");var subQ1=sQuery(id+"F0.wireOp",EDGE,"E332");var subQ2=makeQuery(id+"F0.imprint","INTERSECT",VERTEX,{"derivedFrom":[subQ1,subQ0]});Q1=makeQuery(id+"F0.imprint","IMPRINT",FACE,{"disambiguationData":[TD([[makeQuery(id+"F0.imprint","IMPRINT",EDGE,{"disambiguationData":[TD([[subQ2,-1.0]])],"derivedFrom":subQ1}),1.0]])]});}
            var Q2;
            {var subQ5=sQuery(id+"F0.wireOp",EDGE,"E337");Q2=makeQuery(id+"F0.imprint","IMPRINT",FACE,{"disambiguationData":[TD([[makeQuery(id+"F0.imprint","IMPRINT",EDGE,{"derivedFrom":subQ5}),1.0]])]});}
            var Q3;
            {var subQ1=sQuery(id+"F0.wireOp",EDGE,"E336");var subQ7=sQuery(id+"F0.wireOp",EDGE,"E369");var subQ9=makeQuery(id+"F0.imprint","INTERSECT",VERTEX,{"derivedFrom":[subQ1,subQ7]});Q3=makeQuery(id+"F0.imprint","IMPRINT",FACE,{"disambiguationData":[TD([[makeQuery(id+"F0.imprint","IMPRINT",EDGE,{"disambiguationData":[TD([[subQ9,-1.0]])],"derivedFrom":subQ1}),1.0]])]});}
            var Q4;
            {var subQ0=sQuery(id+"F0.wireOp",EDGE,"E366");var subQ1=sQuery(id+"F0.wireOp",EDGE,"E336");var subQ2=makeQuery(id+"F0.imprint","INTERSECT",VERTEX,{"derivedFrom":[subQ1,subQ0]});Q4=makeQuery(id+"F0.imprint","IMPRINT",FACE,{"disambiguationData":[TD([[makeQuery(id+"F0.imprint","IMPRINT",EDGE,{"disambiguationData":[TD([[subQ2,-1.0]])],"derivedFrom":subQ1}),1.0]])]});}
            var Q5;
            {var subQ5=sQuery(id+"F0.wireOp",EDGE,"E316");var subQ14=makeQuery(id+"F0.imprint","IMPRINT",VERTEX,{"disambiguationData":[OD(0.0)],"derivedFrom":subQ5});Q5=makeQuery(id+"F0.imprint","IMPRINT",FACE,{"disambiguationData":[TD([[makeQuery(id+"F0.imprint","IMPRINT",EDGE,{"disambiguationData":[TD([[subQ14,-1.0]])],"derivedFrom":subQ5}),1.0]])]});}
            var Q6;
            Q6=makeQuery(id+"F0.imprint","IMPRINT",FACE,{"disambiguationData":[TD([[makeQuery(id+"F0.imprint","IMPRINT",EDGE,{"derivedFrom":sQuery(id+"F0.wireOp",EDGE,"E408")}),-1.0]])]});
            var Q7;
            {var subQ3=sQuery(id+"F0.wireOp",EDGE,"E332");var subQ6=sQuery(id+"F0.wireOp",EDGE,"E334");var subQ9=makeQuery(id+"F0.imprint","INTERSECT",VERTEX,{"derivedFrom":[subQ3,subQ6]});Q7=makeQuery(id+"F0.imprint","IMPRINT",FACE,{"disambiguationData":[TD([[makeQuery(id+"F0.imprint","IMPRINT",EDGE,{"disambiguationData":[TD([[subQ9,-1.0]])],"derivedFrom":subQ3}),-1.0]])]});}
            var Q8;
            {var subQ0=sQuery(id+"F0.wireOp",EDGE,"E405");Q8=makeQuery(id+"F0.imprint","IMPRINT",FACE,{"disambiguationData":[TD([[makeQuery(id+"F0.imprint","IMPRINT",EDGE,{"derivedFrom":subQ0}),-1.0]])]});}
            var Q9;
            {var subQ11=sQuery(id+"F0.wireOp",EDGE,"E243");Q9=makeQuery(id+"F0.imprint","IMPRINT",FACE,{"disambiguationData":[TD([[makeQuery(id+"F0.imprint","IMPRINT",EDGE,{"derivedFrom":subQ11}),-1.0]])]});}
            var Q10;
            {var subQ0=sQuery(id+"F0.wireOp",EDGE,"E353");Q10=makeQuery(id+"F0.imprint","IMPRINT",FACE,{"disambiguationData":[TD([[makeQuery(id+"F0.imprint","IMPRINT",EDGE,{"derivedFrom":subQ0}),1.0]])]});}
            var Q11;
            {var subQ0=sQuery(id+"F0.wireOp",EDGE,"E354");Q11=makeQuery(id+"F0.imprint","IMPRINT",FACE,{"disambiguationData":[TD([[makeQuery(id+"F0.imprint","IMPRINT",EDGE,{"derivedFrom":subQ0}),-1.0]])]});}
            var Q12;
            {var subQ0=sQuery(id+"F0.wireOp",EDGE,"E337");Q12=makeQuery(id+"F0.imprint","IMPRINT",FACE,{"disambiguationData":[TD([[makeQuery(id+"F0.imprint","IMPRINT",EDGE,{"derivedFrom":subQ0}),-1.0]])]});}
            var Q13;
            {var subQ4=sQuery(id+"F0.wireOp",EDGE,"E365");Q13=makeQuery(id+"F0.imprint","IMPRINT",FACE,{"disambiguationData":[TD([[makeQuery(id+"F0.imprint","IMPRINT",EDGE,{"derivedFrom":subQ4}),-1.0]])]});}
            var Q14;
            {var subQ5=sQuery(id+"F0.wireOp",EDGE,"E369");var subQ8=sQuery(id+"F0.wireOp",EDGE,"E333");var subQ11=makeQuery(id+"F0.imprint","INTERSECT",VERTEX,{"derivedFrom":[subQ8,subQ5]});Q14=makeQuery(id+"F0.imprint","IMPRINT",FACE,{"disambiguationData":[TD([[makeQuery(id+"F0.imprint","IMPRINT",EDGE,{"disambiguationData":[TD([[subQ11,1.0]])],"derivedFrom":subQ8}),1.0]])]});}
            var Q15;
            {var subQ0=sQuery(id+"F0.wireOp",EDGE,"E354");Q15=makeQuery(id+"F0.imprint","IMPRINT",FACE,{"disambiguationData":[TD([[makeQuery(id+"F0.imprint","IMPRINT",EDGE,{"derivedFrom":subQ0}),1.0]])]});}
            var Q16;
            Q16=makeQuery(id+"F0.imprint","IMPRINT",FACE,{"disambiguationData":[TD([[makeQuery(id+"F0.imprint","IMPRINT",EDGE,{"derivedFrom":sQuery(id+"F0.wireOp",EDGE,"E404")}),1.0]])]});
            var Q17;
            {var subQ2=sQuery(id+"F0.wireOp",EDGE,"E351");Q17=makeQuery(id+"F0.imprint","IMPRINT",FACE,{"disambiguationData":[TD([[makeQuery(id+"F0.imprint","IMPRINT",EDGE,{"derivedFrom":subQ2}),-1.0]])]});}
            var Q18;
            {var subQ0=sQuery(id+"F0.wireOp",EDGE,"E351");Q18=makeQuery(id+"F0.imprint","IMPRINT",FACE,{"disambiguationData":[TD([[makeQuery(id+"F0.imprint","IMPRINT",EDGE,{"derivedFrom":subQ0}),1.0]])]});}
            var Q19;
            Q19=makeQuery(id+"F0.imprint","IMPRINT",FACE,{"disambiguationData":[TD([[makeQuery(id+"F0.imprint","IMPRINT",EDGE,{"derivedFrom":sQuery(id+"F0.wireOp",EDGE,"E404")}),-1.0]])]});
            var Q20;
            {var subQ1=sQuery(id+"F0.wireOp",EDGE,"E137");Q20=makeQuery(id+"F0.imprint","IMPRINT",FACE,{"disambiguationData":[TD([[makeQuery(id+"F0.imprint","IMPRINT",EDGE,{"derivedFrom":subQ1}),1.0]])]});}
            var Q21;
            {var subQ8=sQuery(id+"F0.wireOp",EDGE,"E393");Q21=makeQuery(id+"F0.imprint","IMPRINT",FACE,{"disambiguationData":[TD([[makeQuery(id+"F0.imprint","IMPRINT",EDGE,{"derivedFrom":subQ8}),1.0]])]});}
            var Q22;
            Q22=makeQuery(id+"F0.imprint","IMPRINT",FACE,{"disambiguationData":[TD([[makeQuery(id+"F0.imprint","IMPRINT",EDGE,{"derivedFrom":sQuery(id+"F0.wireOp",EDGE,"E135")}),-1.0]])]});
            var Q23;
            {var subQ3=sQuery(id+"F0.wireOp",EDGE,"E241");Q23=makeQuery(id+"F0.imprint","IMPRINT",FACE,{"disambiguationData":[TD([[makeQuery(id+"F0.imprint","IMPRINT",EDGE,{"derivedFrom":subQ3}),1.0]])]});}
            extrude(context, id + "F1", {"entities" : qUnion([Q0, Q1, Q2, Q3, Q4, Q5, Q6, Q7, Q8, Q9, Q10, Q11, Q12, Q13, Q14, Q15, Q16, Q17, Q18, Q19, Q20, Q21, Q22, Q23]), "depth" : 3 * mm});
        }
        {
            var Q0;
            Q0=makeQuery(id+"F1.opExtrude","SWEPT_FACE",FACE,{"disambiguationData":[OSD([sQuery(id+"F0.wireOp",EDGE,"E335")])]});
            extrude(context, id + "F2", {"entities" : qUnion([Q0]), "operationType" : NewBodyOperationType.ADD, "depth" : 10 * mm});
        }
        {
            var Q0;
            Q0=makeQuery(id+"F1.opExtrude","SWEPT_FACE",FACE,{"disambiguationData":[OSD([sQuery(id+"F0.wireOp",EDGE,"E244")])]});
            extrude(context, id + "F3", {"entities" : qUnion([Q0]), "operationType" : NewBodyOperationType.ADD, "depth" : 10 * mm});
        }
    });
